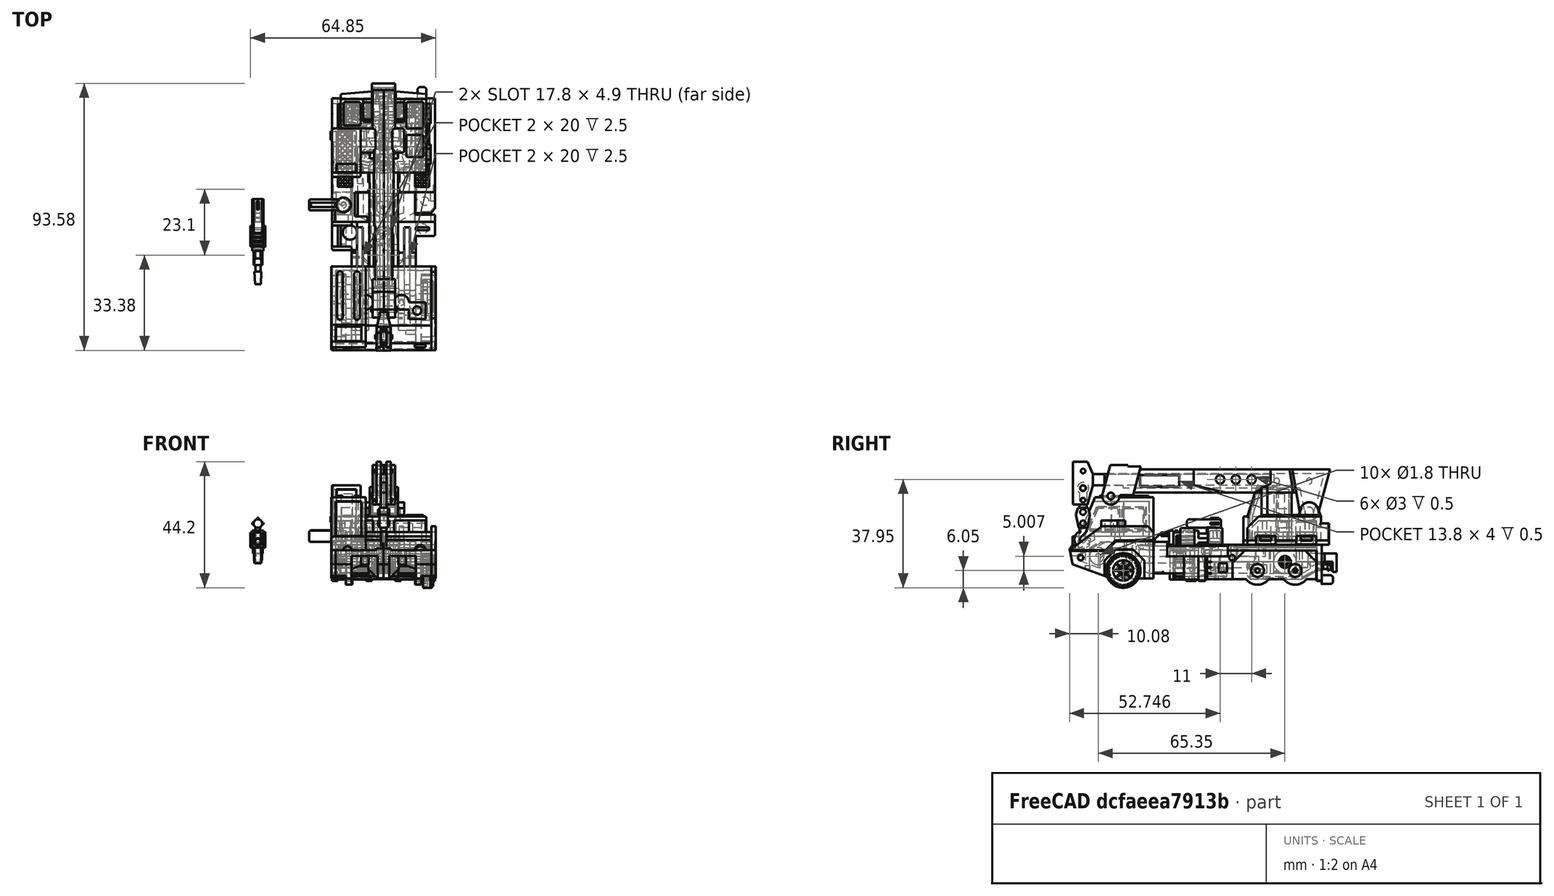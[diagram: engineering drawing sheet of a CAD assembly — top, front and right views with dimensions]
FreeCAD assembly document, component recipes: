
FREECAD ASSEMBLY — COMPONENT RECIPES ("Hook")

This assembly document has 27 components, labeled P0..P26 below (a component is one placed body or linked part). 27 of them carry a construction recipe — the FreeCAD feature program that regenerates the part from scratch, quoted from this document or its linked companion documents; the rest are supplied as boundary geometry only. No exploded tour is included for this assembly.
NOTE — this tour is split across 5 documents so each fits a 32k-token context. This is document 1: the component sections continue in the remaining 4 documents, each repeating the header above.
COMPONENT P0 — recipe-attached ("Rear_Torso", modeled in this document).
Construction recipe (the document's own serialized feature program — sketch geometry with constraints, then the solid features built on it; lengths are millimeters unless a unit is written):

FEATURE [Sketcher::SketchObject] Sketch
  ArcFitTolerance = 1e-06
  AttachmentSupport = -> [XY_Plane]
  FullyConstrained = true
  MakeInternals = false
  MapMode = 5
  sketch-geometry (4):
    g0: LineSegment StartX=0 StartY=0 StartZ=0 EndX=36 EndY=0 EndZ=0
    g1: LineSegment StartX=36 StartY=0 StartZ=0 EndX=36 EndY=43.2 EndZ=0
    g2: LineSegment StartX=36 StartY=43.2 StartZ=0 EndX=0 EndY=43.2 EndZ=0
    g3: LineSegment StartX=0 StartY=43.2 StartZ=0 EndX=0 EndY=0 EndZ=0
  constraints (11):
    c: Coincident(g0,g1)
    c: Coincident(g1,g2)
    c: Coincident(g2,g3)
    c: Coincident(g3,g0)
    c: Horizontal(g0)
    c: Horizontal(g2)
    c: Vertical(g1)
    c: Vertical(g3)
    c: Coincident(g0,g-1)
    c: DistanceY(g1,g1) = 43.2
    c: DistanceX(g2,g2) = 36
FEATURE [PartDesign::Pad] Pad
  Direction = (0,0,1)
  Length = 2
  Length2 = 10
  Profile = -> Sketch
  ReferenceAxis = -> Sketch [N_Axis]
  Refine = true
  Suppressed = false
  Type = 0
FEATURE [Sketcher::SketchObject] Sketch001
  ArcFitTolerance = 1e-06
  AttachmentSupport = -> [Pad]
  ExternalGeometry = -> [Pad]
  FullyConstrained = true
  MakeInternals = false
  MapMode = 5
  Placement = pos=(0,0,2) rot=(0,0,1;0rad)
  sketch-geometry (18):
    g0: LineSegment StartX=13.9 StartY=43.2 StartZ=0 EndX=13.9 EndY=41.4 EndZ=0
    g1: LineSegment StartX=13.9 StartY=41.4 StartZ=0 EndX=22.1 EndY=41.4 EndZ=0
    g2: LineSegment StartX=22.1 StartY=41.4 StartZ=0 EndX=22.1 EndY=43.2 EndZ=0
    g3: LineSegment StartX=22.1 StartY=43.2 StartZ=0 EndX=13.9 EndY=43.2 EndZ=0
    g4: LineSegment StartX=36 StartY=10.3 StartZ=0 EndX=23.6 EndY=10.3 EndZ=0
    g5: LineSegment StartX=23.6 StartY=10.3 StartZ=0 EndX=23.6 EndY=11.3 EndZ=0
    g6: ArcOfCircle CenterX=23.6 CenterY=12.55 CenterZ=0 NormalX=0 NormalY=0 NormalZ=1 AngleXU=0 Radius=1.25 StartAngle=1.5708 EndAngle=4.71239
    g7: LineSegment StartX=23.6 StartY=13.8 StartZ=0 EndX=23.6 EndY=18 EndZ=0
    g8: ArcOfCircle CenterX=18.1 CenterY=18 CenterZ=0 NormalX=0 NormalY=0 NormalZ=1 AngleXU=0 Radius=5.5 StartAngle=2e-16 EndAngle=3.14159
    g9: LineSegment StartX=12.6 StartY=18 StartZ=0 EndX=12.6 EndY=13.8 EndZ=0
    g10: ArcOfCircle CenterX=12.6 CenterY=12.55 CenterZ=0 NormalX=0 NormalY=0 NormalZ=1 AngleXU=0 Radius=1.25 StartAngle=4.71239 EndAngle=7.85398
    g11: LineSegment StartX=12.6 StartY=11.3 StartZ=0 EndX=12.6 EndY=10.3 EndZ=0
    g12: LineSegment StartX=12.6 StartY=10.3 StartZ=0 EndX=8 EndY=10.3 EndZ=0
    g13: LineSegment StartX=8 StartY=10.3 StartZ=0 EndX=8 EndY=1.8 EndZ=0
    g14: LineSegment StartX=8 StartY=1.8 StartZ=0 EndX=12.4 EndY=1.8 EndZ=0
    g15: LineSegment StartX=12.4 StartY=0 StartZ=0 EndX=36 EndY=0 EndZ=0
    g16: LineSegment StartX=36 StartY=0 StartZ=0 EndX=36 EndY=10.3 EndZ=0
    g17: LineSegment StartX=12.4 StartY=1.8 StartZ=0 EndX=12.4 EndY=0 EndZ=0
  constraints (58):
    c: Coincident(g0,g1)
    c: Coincident(g1,g2)
    c: Coincident(g2,g3)
    c: Coincident(g3,g0)
    c: Vertical(g0)
    c: Vertical(g2)
    c: Horizontal(g1)
    c: Horizontal(g3)
    c: PointOnObject(g0,g-3)
    c: DistanceX(g-3,g-3) = 36
    c: DistanceX(g-3,g0) = 13.9
    c: DistanceX(g2,g-3) = 13.9
    c: DistanceX(g0,g2) = 8.2
    c: DistanceY(g0,g0) = 1.8
    c: PointOnObject(g4,g-4)
    c: Horizontal(g4)
    c: DistanceY(g4,g-4) = 32.9
    c: DistanceX(g4,g4) = 12.4
    c: Coincident(g5,g4)
    c: Vertical(g5)
    c: Coincident(g6,g5)
    c: Coincident(g7,g6)
    c: Vertical(g7)
    c: Coincident(g8,g7)
    c: Coincident(g9,g8)
    c: Vertical(g9)
    c: Coincident(g10,g9)
    c: Coincident(g11,g10)
    c: Vertical(g11)
    c: Coincident(g12,g11)
    c: Horizontal(g12)
    c: Coincident(g13,g12)
    c: Vertical(g13)
    c: Coincident(g14,g13)
    c: Horizontal(g14)
    c: PointOnObject(g15,g-5)
    c: Coincident(g15,g-5)
    c: Coincident(g16,g15)
    c: Coincident(g16,g4)
    c: Diameter(g6) = 2.5
    c: Diameter(g10) = 2.5
    c: Diameter(g8) = 11
    c: DistanceX(g11,g4) = 11
    c: DistanceX(g6,g6) = 0
    c: DistanceX(g5,g6) = 0
    c: DistanceX(g10,g9) = 0
    c: DistanceX(g10,g10) = 0
    c: DistanceX(g-1,g13) = 8
    c: DistanceX(g13,g14) = 4.4
    c: Coincident(g17,g14)
    c: Coincident(g17,g15)
    c: Vertical(g17)
    c: DistanceY(g17,g17) = 1.8
    c: DistanceY(g15,g8) = 18
    c: DistanceY(g5,g5) = 1
    c: DistanceY(g11,g11) = 1
    c: DistanceY(g8,g7) = 0
    c: DistanceY(g12,g-6) = 32.9
FEATURE [PartDesign::Pocket] Pocket
  BaseFeature = -> Pad
  Direction = (0,0,-1)
  Length = 5
  Length2 = 5
  Profile = -> Sketch001
  ReferenceAxis = -> Sketch001 [N_Axis]
  Refine = true
  Suppressed = false
  Type = 0
FEATURE [Sketcher::SketchObject] Sketch002
  ArcFitTolerance = 1e-06
  AttachmentSupport = -> [Pocket]
  ExternalGeometry = -> [Pocket]
  FullyConstrained = true
  MakeInternals = false
  MapMode = 5
  Placement = pos=(0,0,2) rot=(0,0,1;0rad)
  sketch-geometry (8):
    g0: LineSegment StartX=2 StartY=41.2 StartZ=0 EndX=2 EndY=12.3 EndZ=0
    g1: LineSegment StartX=2 StartY=12.3 StartZ=0 EndX=7 EndY=12.3 EndZ=0
    g2: LineSegment StartX=7 StartY=12.3 StartZ=0 EndX=7 EndY=41.2 EndZ=0
    g3: LineSegment StartX=7 StartY=41.2 StartZ=0 EndX=2 EndY=41.2 EndZ=0
    g4: LineSegment StartX=29 StartY=41.2 StartZ=0 EndX=29 EndY=12.3 EndZ=0
    g5: LineSegment StartX=29 StartY=12.3 StartZ=0 EndX=34 EndY=12.3 EndZ=0
    g6: LineSegment StartX=34 StartY=12.3 StartZ=0 EndX=34 EndY=41.2 EndZ=0
    g7: LineSegment StartX=34 StartY=41.2 StartZ=0 EndX=29 EndY=41.2 EndZ=0
  constraints (25):
    c: Coincident(g0,g1)
    c: Coincident(g1,g2)
    c: Coincident(g2,g3)
    c: Coincident(g3,g0)
    c: Vertical(g0)
    c: Vertical(g2)
    c: Horizontal(g1)
    c: Horizontal(g3)
    c: Coincident(g4,g5)
    c: Coincident(g5,g6)
    c: Coincident(g6,g7)
    c: Coincident(g7,g4)
    c: Vertical(g4)
    c: Vertical(g6)
    c: Horizontal(g5)
    c: Horizontal(g7)
    c: DistanceX(g3,g3) = 5
    c: DistanceX(g7,g7) = 5
    c: DistanceX(g-6,g0) = 2
    c: DistanceX(g6,g-4) = 2
    c: DistanceY(g6,g-4) = 2
    c: DistanceY(g0,g-6) = 2
    c: DistanceY(g-3,g5) = 2
    c: DistanceY(g-7,g1) = 2
    c: DistanceY(g0,g0) = 28.9
FEATURE [PartDesign::Pocket] Pocket001
  BaseFeature = -> Pocket
  Direction = (0,0,-1)
  Length = 0.5
  Length2 = 5
  Profile = -> Sketch002
  ReferenceAxis = -> Sketch002 [N_Axis]
  Refine = true
  Suppressed = false
  Type = 0
FEATURE [Sketcher::SketchObject] Sketch003
  ArcFitTolerance = 1e-06
  AttachmentSupport = -> [Pocket001]
  ExternalGeometry = -> [Pocket001]
  FullyConstrained = true
  MakeInternals = false
  MapMode = 5
  Placement = pos=(0,0,1.5) rot=(0,0,1;0rad)
  sketch-geometry (36):
    g0: LineSegment StartX=30.625 StartY=41.2 StartZ=0 EndX=29.875 EndY=40.45 EndZ=0
    g1: LineSegment StartX=29.875 StartY=40.45 StartZ=0 EndX=30.625 EndY=39.7 EndZ=0
    g2: LineSegment StartX=30.625 StartY=39.7 StartZ=0 EndX=31.375 EndY=40.45 EndZ=0
    g3: LineSegment StartX=31.375 StartY=40.45 StartZ=0 EndX=30.625 EndY=41.2 EndZ=0
    g4: LineSegment [constr] StartX=29.875 StartY=40.45 StartZ=0 EndX=31.375 EndY=40.45 EndZ=0
    g5: LineSegment [constr] StartX=30.625 StartY=41.2 StartZ=0 EndX=30.625 EndY=39.7 EndZ=0
    g6: LineSegment StartX=31.625 StartY=40.45 StartZ=0 EndX=32.375 EndY=41.2 EndZ=0
    g7: LineSegment StartX=32.375 StartY=41.2 StartZ=0 EndX=33.125 EndY=40.45 EndZ=0
    g8: LineSegment StartX=33.125 StartY=40.45 StartZ=0 EndX=32.375 EndY=39.7 EndZ=0
    g9: LineSegment StartX=32.375 StartY=39.7 StartZ=0 EndX=31.625 EndY=40.45 EndZ=0
    g10: LineSegment [constr] StartX=32.375 StartY=41.2 StartZ=0 EndX=32.375 EndY=39.7 EndZ=0
    g11: LineSegment [constr] StartX=31.625 StartY=40.45 StartZ=0 EndX=33.125 EndY=40.45 EndZ=0
    g12: LineSegment StartX=29.625 StartY=40.45 StartZ=0 EndX=29 EndY=41.075 EndZ=0
    g13: LineSegment StartX=29 StartY=41.075 StartZ=0 EndX=29 EndY=39.825 EndZ=0
    g14: LineSegment StartX=29 StartY=39.825 StartZ=0 EndX=29.625 EndY=40.45 EndZ=0
    g15: LineSegment StartX=33.375 StartY=40.45 StartZ=0 EndX=34 EndY=41.075 EndZ=0
    g16: LineSegment StartX=34 StartY=41.075 StartZ=0 EndX=34 EndY=39.825 EndZ=0
    g17: LineSegment StartX=34 StartY=39.825 StartZ=0 EndX=33.375 EndY=40.45 EndZ=0
    g18: LineSegment StartX=3.625 StartY=41.2 StartZ=0 EndX=2.875 EndY=40.45 EndZ=0
    g19: LineSegment StartX=2.875 StartY=40.45 StartZ=0 EndX=3.625 EndY=39.7 EndZ=0
    g20: LineSegment StartX=3.625 StartY=39.7 StartZ=0 EndX=4.375 EndY=40.45 EndZ=0
    g21: LineSegment StartX=4.375 StartY=40.45 StartZ=0 EndX=3.625 EndY=41.2 EndZ=0
    g22: LineSegment [constr] StartX=2.875 StartY=40.45 StartZ=0 EndX=4.375 EndY=40.45 EndZ=0
    g23: LineSegment [constr] StartX=3.625 StartY=41.2 StartZ=0 EndX=3.625 EndY=39.7 EndZ=0
    g24: LineSegment StartX=4.625 StartY=40.45 StartZ=0 EndX=5.375 EndY=41.2 EndZ=0
    g25: LineSegment StartX=5.375 StartY=41.2 StartZ=0 EndX=6.125 EndY=40.45 EndZ=0
    g26: LineSegment StartX=6.125 StartY=40.45 StartZ=0 EndX=5.375 EndY=39.7 EndZ=0
    g27: LineSegment StartX=5.375 StartY=39.7 StartZ=0 EndX=4.625 EndY=40.45 EndZ=0
    g28: LineSegment [constr] StartX=5.375 StartY=41.2 StartZ=0 EndX=5.375 EndY=39.7 EndZ=0
    g29: LineSegment [constr] StartX=4.625 StartY=40.45 StartZ=0 EndX=6.125 EndY=40.45 EndZ=0
    g30: LineSegment StartX=2.625 StartY=40.45 StartZ=0 EndX=2 EndY=41.075 EndZ=0
    g31: LineSegment StartX=2 StartY=41.075 StartZ=0 EndX=2 EndY=39.825 EndZ=0
    g32: LineSegment StartX=2 StartY=39.825 StartZ=0 EndX=2.625 EndY=40.45 EndZ=0
    g33: LineSegment StartX=6.375 StartY=40.45 StartZ=0 EndX=7 EndY=41.075 EndZ=0
    g34: LineSegment StartX=7 StartY=41.075 StartZ=0 EndX=7 EndY=39.825 EndZ=0
    g35: LineSegment StartX=7 StartY=39.825 StartZ=0 EndX=6.375 EndY=40.45 EndZ=0
  constraints (101):
    c: DistanceX(g-3,g-3) = 5
    c: Coincident(g2,g1)
    c: Coincident(g3,g2)
    c: Coincident(g3,g0)
    c: Coincident(g4,g0)
    c: Coincident(g4,g2)
    c: Coincident(g5,g0)
    c: Coincident(g5,g1)
    c: Horizontal(g4)
    c: Vertical(g5)
    c: DistanceX(g4,g4) = 1.5
    c: Angle(g3,g2) = 1.5708
    c: Angle(g0,g3) = 1.5708
    c: Angle(g2,g1) = 1.5708
    c: Coincident(g1,g0)
    c: Coincident(g7,g6)
    c: Coincident(g8,g7)
    c: Coincident(g9,g8)
    c: Coincident(g9,g6)
    c: Coincident(g10,g6)
    c: Coincident(g10,g8)
    c: Coincident(g11,g6)
    c: Coincident(g11,g7)
    c: Horizontal(g11)
    c: Vertical(g10)
    c: DistanceX(g11,g11) = 1.5
    c: Angle(g7,g8) = 1.5708
    c: Angle(g6,g7) = 1.5708
    c: Angle(g8,g9) = 1.5708
    c: DistanceX(g2,g6) = 0.25
    c: DistanceY(g2,g6) = 0
    c: Coincident(g13,g12)
    c: Vertical(g13)
    c: Coincident(g14,g13)
    c: Coincident(g14,g12)
    c: DistanceX(g12,g0) = 0.25
    c: DistanceY(g12,g0) = 0
    c: Angle(g12,g14) = 1.5708
    c: Coincident(g16,g15)
    c: Vertical(g16)
    c: Coincident(g17,g16)
    c: Coincident(g17,g15)
    c: DistanceX(g7,g15) = 0.25
    c: DistanceY(g15,g7) = 0
    c: Angle(g17,g15) = 1.5708
    c: Angle(g13,g12) = 0.785398
    c: Angle(g15,g16) = 0.785398
    c: DistanceX(g15,g15) = 0.625
    c: DistanceX(g12,g12) = 0.625
    c: Coincident(g20,g19)
    c: Coincident(g21,g20)
    c: Coincident(g21,g18)
    c: Coincident(g22,g18)
    c: Coincident(g22,g20)
    c: Coincident(g23,g18)
    c: Coincident(g23,g19)
    c: Horizontal(g22)
    c: Vertical(g23)
    c: DistanceX(g22,g22) = 1.5
    c: Angle(g21,g20) = 1.5708
    c: Angle(g18,g21) = 1.5708
    c: Angle(g20,g19) = 1.5708
    c: Coincident(g19,g18)
    c: Coincident(g25,g24)
    c: Coincident(g26,g25)
    c: Coincident(g27,g26)
    c: Coincident(g27,g24)
    c: Coincident(g28,g24)
    c: Coincident(g28,g26)
    c: Coincident(g29,g24)
    c: Coincident(g29,g25)
    c: Horizontal(g29)
    c: Vertical(g28)
    c: DistanceX(g29,g29) = 1.5
    c: Angle(g25,g26) = 1.5708
    c: Angle(g24,g25) = 1.5708
    c: Angle(g26,g27) = 1.5708
    c: DistanceX(g20,g24) = 0.25
    c: DistanceY(g20,g24) = 0
    c: Coincident(g31,g30)
    c: Vertical(g31)
    c: Coincident(g32,g31)
    c: Coincident(g32,g30)
    c: DistanceX(g30,g18) = 0.25
    c: DistanceY(g30,g18) = 0
    c: Angle(g30,g32) = 1.5708
    c: Coincident(g34,g33)
    c: Vertical(g34)
    c: Coincident(g35,g34)
    c: Coincident(g35,g33)
    c: DistanceX(g25,g33) = 0.25
    c: DistanceY(g33,g25) = 0
    c: Angle(g35,g33) = 1.5708
    c: Angle(g31,g30) = 0.785398
    c: Angle(g33,g34) = 0.785398
    c: DistanceX(g33,g33) = 0.625
    c: DistanceX(g30,g30) = 0.625
    c: PointOnObject(g0,g-5)
    c: PointOnObject(g12,g-6)
    c: PointOnObject(g18,g-3)
    c: PointOnObject(g30,g-4)
FEATURE [PartDesign::Pocket] Pocket002
  BaseFeature = -> Pocket001
  Direction = (0,0,-1)
  Length = 0.5
  Length2 = 5
  Profile = -> Sketch003
  ReferenceAxis = -> Sketch003 [N_Axis]
  Refine = true
  Suppressed = false
  Type = 0
FEATURE [PartDesign::LinearPattern] LinearPattern
  BaseFeature = -> Pocket002
  Direction = -> Sketch003 [V_Axis]
  Length = 27.398
  Mode = 1
  Occurrences = 15
  Offset = 1.957
  Originals = -> [Pocket002]
  Refine = true
  Reversed = true
  Suppressed = false
  TransformMode = 0
FEATURE [Sketcher::SketchObject] Sketch004
  ArcFitTolerance = 1e-06
  AttachmentSupport = -> [LinearPattern]
  ExternalGeometry = -> [LinearPattern]
  FullyConstrained = true
  MakeInternals = false
  MapMode = 5
  Placement = pos=(0,0,1.5) rot=(0,0,1;0rad)
  sketch-geometry (36):
    g0: LineSegment StartX=2.125 StartY=41.2 StartZ=0 EndX=3.375 EndY=41.2 EndZ=0
    g1: LineSegment StartX=3.375 StartY=41.2 StartZ=0 EndX=2.75 EndY=40.575 EndZ=0
    g2: LineSegment StartX=2.75 StartY=40.575 StartZ=0 EndX=2.125 EndY=41.2 EndZ=0
    g3: LineSegment StartX=3.875 StartY=41.2 StartZ=0 EndX=5.125 EndY=41.2 EndZ=0
    g4: LineSegment StartX=5.125 StartY=41.2 StartZ=0 EndX=4.5 EndY=40.575 EndZ=0
    g5: LineSegment StartX=4.5 StartY=40.575 StartZ=0 EndX=3.875 EndY=41.2 EndZ=0
    g6: LineSegment StartX=5.625 StartY=41.2 StartZ=0 EndX=6.875 EndY=41.2 EndZ=0
    g7: LineSegment StartX=6.875 StartY=41.2 StartZ=0 EndX=6.25 EndY=40.575 EndZ=0
    g8: LineSegment StartX=6.25 StartY=40.575 StartZ=0 EndX=5.625 EndY=41.2 EndZ=0
    g9: LineSegment StartX=6.877 StartY=12.3 StartZ=0 EndX=5.623 EndY=12.3 EndZ=0
    g10: LineSegment StartX=5.623 StartY=12.3 StartZ=0 EndX=6.25 EndY=12.927 EndZ=0
    g11: LineSegment StartX=6.25 StartY=12.927 StartZ=0 EndX=6.877 EndY=12.3 EndZ=0
    g12: LineSegment StartX=3.873 StartY=12.3 StartZ=0 EndX=5.127 EndY=12.3 EndZ=0
    g13: LineSegment StartX=5.127 StartY=12.3 StartZ=0 EndX=4.5 EndY=12.927 EndZ=0
    g14: LineSegment StartX=4.5 StartY=12.927 StartZ=0 EndX=3.873 EndY=12.3 EndZ=0
    g15: LineSegment StartX=3.377 StartY=12.3 StartZ=0 EndX=2.123 EndY=12.3 EndZ=0
    g16: LineSegment StartX=2.123 StartY=12.3 StartZ=0 EndX=2.75 EndY=12.927 EndZ=0
    g17: LineSegment StartX=2.75 StartY=12.927 StartZ=0 EndX=3.377 EndY=12.3 EndZ=0
    g18: LineSegment StartX=29.125 StartY=41.2 StartZ=0 EndX=30.375 EndY=41.2 EndZ=0
    g19: LineSegment StartX=30.375 StartY=41.2 StartZ=0 EndX=29.75 EndY=40.575 EndZ=0
    g20: LineSegment StartX=29.75 StartY=40.575 StartZ=0 EndX=29.125 EndY=41.2 EndZ=0
    g21: LineSegment StartX=30.875 StartY=41.2 StartZ=0 EndX=32.125 EndY=41.2 EndZ=0
    g22: LineSegment StartX=32.125 StartY=41.2 StartZ=0 EndX=31.5 EndY=40.575 EndZ=0
    g23: LineSegment StartX=31.5 StartY=40.575 StartZ=0 EndX=30.875 EndY=41.2 EndZ=0
    g24: LineSegment StartX=32.625 StartY=41.2 StartZ=0 EndX=33.875 EndY=41.2 EndZ=0
    g25: LineSegment StartX=33.875 StartY=41.2 StartZ=0 EndX=33.25 EndY=40.575 EndZ=0
    g26: LineSegment StartX=33.25 StartY=40.575 StartZ=0 EndX=32.625 EndY=41.2 EndZ=0
    g27: LineSegment StartX=29.123 StartY=12.3 StartZ=0 EndX=30.377 EndY=12.3 EndZ=0
    g28: LineSegment StartX=30.377 StartY=12.3 StartZ=0 EndX=29.75 EndY=12.927 EndZ=0
    g29: LineSegment StartX=29.75 StartY=12.927 StartZ=0 EndX=29.123 EndY=12.3 EndZ=0
    g30: LineSegment StartX=30.873 StartY=12.3 StartZ=0 EndX=32.127 EndY=12.3 EndZ=0
    g31: LineSegment StartX=32.127 StartY=12.3 StartZ=0 EndX=31.5 EndY=12.927 EndZ=0
    g32: LineSegment StartX=31.5 StartY=12.927 StartZ=0 EndX=30.873 EndY=12.3 EndZ=0
    g33: LineSegment StartX=32.623 StartY=12.3 StartZ=0 EndX=33.877 EndY=12.3 EndZ=0
    g34: LineSegment StartX=33.877 StartY=12.3 StartZ=0 EndX=33.25 EndY=12.927 EndZ=0
    g35: LineSegment StartX=33.25 StartY=12.927 StartZ=0 EndX=32.623 EndY=12.3 EndZ=0
  constraints (109):
    c: PointOnObject(g0,g-5)
    c: PointOnObject(g0,g-5)
    c: Coincident(g1,g0)
    c: Coincident(g2,g1)
    c: Coincident(g2,g0)
    c: DistanceX(g-4,g-3) = 0.25
    c: DistanceX(g-4,g1) = 0.125
    c: DistanceY(g-4,g1) = 0.125
    c: Parallel(g1,g-3)
    c: Parallel(g2,g-4)
    c: PointOnObject(g3,g-6)
    c: PointOnObject(g3,g-6)
    c: Coincident(g4,g3)
    c: Coincident(g5,g4)
    c: Coincident(g5,g3)
    c: PointOnObject(g6,g-9)
    c: PointOnObject(g6,g-9)
    c: Coincident(g7,g6)
    c: Coincident(g8,g7)
    c: Coincident(g8,g6)
    c: DistanceX(g-7,g4) = 0.125
    c: DistanceX(g-10,g7) = 0.125
    c: Parallel(g-7,g5)
    c: Parallel(g4,g-8)
    c: Parallel(g-10,g8)
    c: Parallel(g7,g-11)
    c: DistanceY(g-7,g4) = 0.125
    c: DistanceY(g-10,g7) = 0.125
    c: PointOnObject(g9,g-14)
    c: PointOnObject(g9,g-14)
    c: Coincident(g10,g9)
    c: Coincident(g11,g10)
    c: Coincident(g11,g9)
    c: PointOnObject(g12,g-14)
    c: PointOnObject(g12,g-14)
    c: Coincident(g13,g12)
    c: Coincident(g14,g13)
    c: Coincident(g14,g12)
    c: PointOnObject(g15,g-14)
    c: PointOnObject(g15,g-14)
    c: Coincident(g16,g15)
    c: Coincident(g17,g16)
    c: Coincident(g17,g15)
    c: Parallel(g-13,g16)
    c: Parallel(g17,g-12)
    c: Parallel(g-16,g14)
    c: Parallel(g13,g-15)
    c: Parallel(g-17,g10)
    c: Parallel(g11,g-18)
    c: DistanceX(g-17,g10) = 0.125
    c: DistanceX(g-16,g13) = 0.125
    c: DistanceX(g16,g-12) = 0.125
    c: DistanceY(g16,g-13) = 0.125
    c: DistanceY(g13,g-16) = 0.125
    c: DistanceY(g10,g-17) = 0.125
    c: PointOnObject(g18,g-19)
    c: PointOnObject(g18,g-19)
    c: Coincident(g19,g18)
    c: Coincident(g20,g19)
    c: Coincident(g20,g18)
    c: PointOnObject(g21,g-22)
    c: PointOnObject(g21,g-22)
    c: Coincident(g22,g21)
    c: Coincident(g23,g22)
    c: Coincident(g23,g21)
    c: PointOnObject(g24,g-25)
    c: PointOnObject(g24,g-25)
    c: Coincident(g25,g24)
    c: Coincident(g26,g25)
    c: Coincident(g26,g24)
    c: Parallel(g-26,g26)
    c: Parallel(g25,g-27)
    c: Parallel(g22,g-24)
    c: Parallel(g23,g-23)
    c: Parallel(g-21,g19)
    c: Parallel(g20,g-20)
    c: DistanceX(g-20,g19) = 0.125
    c: DistanceX(g-23,g22) = 0.125
    c: DistanceX(g-26,g25) = 0.125
    c: DistanceY(g-26,g25) = 0.125
    c: DistanceY(g-23,g22) = 0.125
    c: DistanceY(g-20,g19) = 0.125
    c: PointOnObject(g27,g-30)
    c: PointOnObject(g27,g-30)
    c: Coincident(g28,g27)
    c: Coincident(g29,g28)
    c: Coincident(g29,g27)
    c: PointOnObject(g30,g-30)
    c: PointOnObject(g30,g-30)
    c: Coincident(g31,g30)
    c: Coincident(g32,g31)
    c: Coincident(g32,g30)
    c: PointOnObject(g33,g-30)
    c: PointOnObject(g33,g-30)
    c: Coincident(g34,g33)
    c: Coincident(g35,g34)
    c: Coincident(g35,g33)
    c: Parallel(g29,g-28)
    c: Parallel(g28,g-29)
    c: Parallel(g32,g-31)
    c: Parallel(g31,g-32)
    c: Parallel(g35,g-33)
    c: Parallel(g34,g-34)
    c: DistanceX(g-28,g28) = 0.125
    c: DistanceX(g-31,g31) = 0.125
    c: DistanceX(g-33,g34) = 0.125
    c: DistanceY(g28,g-28) = 0.125
    c: DistanceY(g31,g-31) = 0.125
    c: DistanceY(g34,g-33) = 0.125
FEATURE [PartDesign::Pocket] Pocket003
  BaseFeature = -> LinearPattern
  Direction = (0,0,-1)
  Length = 0.5
  Length2 = 5
  Profile = -> Sketch004
  ReferenceAxis = -> Sketch004 [N_Axis]
  Refine = true
  Suppressed = false
  Type = 0
FEATURE [Sketcher::SketchObject] Sketch005
  ArcFitTolerance = 1e-06
  AttachmentSupport = -> [Pocket003]
  ExternalGeometry = -> [Pocket003]
  FullyConstrained = true
  MakeInternals = false
  MapMode = 5
  Placement = pos=(0,0,1.5) rot=(0,0,1;0rad)
  sketch-geometry (36):
    g0: LineSegment StartX=2.75 StartY=40.22 StartZ=0 EndX=2 EndY=39.47 EndZ=0
    g1: LineSegment StartX=2 StartY=39.47 StartZ=0 EndX=2.75 EndY=38.72 EndZ=0
    g2: LineSegment StartX=2.75 StartY=38.72 StartZ=0 EndX=3.5 EndY=39.47 EndZ=0
    g3: LineSegment StartX=3.5 StartY=39.47 StartZ=0 EndX=2.75 EndY=40.22 EndZ=0
    g4: LineSegment StartX=4.5 StartY=40.22 StartZ=0 EndX=3.75 EndY=39.47 EndZ=0
    g5: LineSegment StartX=3.75 StartY=39.47 StartZ=0 EndX=4.5 EndY=38.72 EndZ=0
    g6: LineSegment StartX=4.5 StartY=38.72 StartZ=0 EndX=5.25 EndY=39.47 EndZ=0
    g7: LineSegment StartX=5.25 StartY=39.47 StartZ=0 EndX=4.5 EndY=40.22 EndZ=0
    g8: LineSegment StartX=6.25 StartY=40.22 StartZ=0 EndX=5.5 EndY=39.47 EndZ=0
    g9: LineSegment StartX=5.5 StartY=39.47 StartZ=0 EndX=6.25 EndY=38.72 EndZ=0
    g10: LineSegment StartX=6.25 StartY=38.72 StartZ=0 EndX=7 EndY=39.47 EndZ=0
    g11: LineSegment StartX=7 StartY=39.47 StartZ=0 EndX=6.25 EndY=40.22 EndZ=0
    g12: LineSegment [constr] StartX=6.25 StartY=40.22 StartZ=0 EndX=6.25 EndY=38.72 EndZ=0
    g13: LineSegment [constr] StartX=4.5 StartY=40.22 StartZ=0 EndX=4.5 EndY=38.72 EndZ=0
    g14: LineSegment [constr] StartX=2.75 StartY=40.22 StartZ=0 EndX=2.75 EndY=38.72 EndZ=0
    g15: LineSegment [constr] StartX=3.5 StartY=39.47 StartZ=0 EndX=2 EndY=39.47 EndZ=0
    g16: LineSegment [constr] StartX=5.25 StartY=39.47 StartZ=0 EndX=3.75 EndY=39.47 EndZ=0
    g17: LineSegment [constr] StartX=7 StartY=39.47 StartZ=0 EndX=5.5 EndY=39.47 EndZ=0
    g18: LineSegment StartX=29.75 StartY=40.22 StartZ=0 EndX=29 EndY=39.47 EndZ=0
    g19: LineSegment StartX=29 StartY=39.47 StartZ=0 EndX=29.75 EndY=38.72 EndZ=0
    g20: LineSegment StartX=29.75 StartY=38.72 StartZ=0 EndX=30.5 EndY=39.47 EndZ=0
    g21: LineSegment StartX=30.5 StartY=39.47 StartZ=0 EndX=29.75 EndY=40.22 EndZ=0
    g22: LineSegment StartX=31.5 StartY=40.22 StartZ=0 EndX=30.75 EndY=39.47 EndZ=0
    g23: LineSegment StartX=30.75 StartY=39.47 StartZ=0 EndX=31.5 EndY=38.72 EndZ=0
    g24: LineSegment StartX=31.5 StartY=38.72 StartZ=0 EndX=32.25 EndY=39.47 EndZ=0
    g25: LineSegment StartX=32.25 StartY=39.47 StartZ=0 EndX=31.5 EndY=40.22 EndZ=0
    g26: LineSegment StartX=33.25 StartY=40.22 StartZ=0 EndX=32.5 EndY=39.47 EndZ=0
    g27: LineSegment StartX=32.5 StartY=39.47 StartZ=0 EndX=33.25 EndY=38.72 EndZ=0
    g28: LineSegment StartX=33.25 StartY=38.72 StartZ=0 EndX=34 EndY=39.47 EndZ=0
    g29: LineSegment StartX=34 StartY=39.47 StartZ=0 EndX=33.25 EndY=40.22 EndZ=0
    g30: LineSegment [constr] StartX=30.5 StartY=39.47 StartZ=0 EndX=29 EndY=39.47 EndZ=0
    g31: LineSegment [constr] StartX=29.75 StartY=40.22 StartZ=0 EndX=29.75 EndY=38.72 EndZ=0
    g32: LineSegment [constr] StartX=31.5 StartY=40.22 StartZ=0 EndX=31.5 EndY=38.72 EndZ=0
    g33: LineSegment [constr] StartX=32.25 StartY=39.47 StartZ=0 EndX=30.75 EndY=39.47 EndZ=0
    g34: LineSegment [constr] StartX=33.25 StartY=40.22 StartZ=0 EndX=33.25 EndY=38.72 EndZ=0
    g35: LineSegment [constr] StartX=34 StartY=39.47 StartZ=0 EndX=32.5 EndY=39.47 EndZ=0
  constraints (97):
    c: Coincident(g1,g0)
    c: Coincident(g2,g1)
    c: Coincident(g3,g2)
    c: Coincident(g3,g0)
    c: Coincident(g5,g4)
    c: Coincident(g6,g5)
    c: Coincident(g7,g6)
    c: Coincident(g7,g4)
    c: Coincident(g9,g8)
    c: Coincident(g10,g9)
    c: Coincident(g11,g10)
    c: Coincident(g11,g8)
    c: Coincident(g12,g8)
    c: Coincident(g12,g9)
    c: Vertical(g12)
    c: Coincident(g13,g4)
    c: Coincident(g13,g5)
    c: Vertical(g13)
    c: Coincident(g14,g0)
    c: Coincident(g14,g1)
    c: Coincident(g15,g2)
    c: Coincident(g15,g0)
    c: Horizontal(g15)
    c: Coincident(g16,g6)
    c: Coincident(g16,g4)
    c: Horizontal(g16)
    c: Coincident(g17,g10)
    c: Coincident(g17,g8)
    c: Horizontal(g17)
    c: Vertical(g14)
    c: DistanceX(g15,g15) = 1.5
    c: DistanceX(g16,g16) = 1.5
    c: DistanceX(g17,g17) = 1.5
    c: Angle(g3,g2) = 1.5708
    c: Angle(g0,g3) = 1.5708
    c: Angle(g2,g1) = 1.5708
    c: Angle(g7,g6) = 1.5708
    c: Angle(g4,g7) = 1.5708
    c: Angle(g6,g5) = 1.5708
    c: Angle(g11,g10) = 1.5708
    c: Angle(g8,g11) = 1.5708
    c: Angle(g10,g9) = 1.5708
    c: PointOnObject(g10,g-15)
    c: PointOnObject(g0,g-16)
    c: DistanceY(g0,g-3) = 0.23
    c: DistanceY(g4,g-8) = 0.23
    c: DistanceY(g8,g-12) = 0.23
    c: DistanceX(g4,g-18) = 0
    c: DistanceY(g-6,g1) = 0.227
    c: Coincident(g19,g18)
    c: Coincident(g20,g19)
    c: Coincident(g21,g20)
    c: Coincident(g21,g18)
    c: Coincident(g23,g22)
    c: Coincident(g24,g23)
    c: Coincident(g25,g24)
    c: Coincident(g25,g22)
    c: Coincident(g27,g26)
    c: Coincident(g28,g27)
    c: Coincident(g29,g28)
    c: Coincident(g29,g26)
    c: Coincident(g30,g20)
    c: Coincident(g30,g18)
    c: Horizontal(g30)
    c: Coincident(g31,g18)
    c: Coincident(g31,g19)
    c: Coincident(g32,g22)
    c: Coincident(g32,g23)
    c: Vertical(g32)
    c: Coincident(g33,g24)
    c: Coincident(g33,g22)
    c: Horizontal(g33)
    c: Coincident(g34,g26)
    c: Coincident(g34,g27)
    c: Vertical(g34)
    c: Coincident(g35,g28)
    c: Coincident(g35,g26)
    c: Horizontal(g35)
    c: Vertical(g31)
    c: DistanceX(g30,g30) = 1.5
    c: DistanceX(g33,g33) = 1.5
    c: DistanceX(g35,g35) = 1.5
    c: Angle(g29,g28) = 1.5708
    c: Angle(g25,g24) = 1.5708
    c: Angle(g21,g20) = 1.5708
    c: Angle(g18,g21) = 1.5708
    c: Angle(g20,g19) = 1.5708
    c: Angle(g22,g25) = 1.5708
    c: Angle(g24,g23) = 1.5708
    c: Angle(g26,g29) = 1.5708
    c: Angle(g28,g27) = 1.5708
    c: PointOnObject(g18,g-32)
    c: PointOnObject(g28,g-33)
    c: DistanceX(g22,g-35) = 0
    c: DistanceY(g18,g-20) = 0.23
    c: DistanceY(g22,g-25) = 0.23
    c: DistanceY(g26,g-29) = 0.23
FEATURE [PartDesign::Pocket] Pocket004
  BaseFeature = -> Pocket003
  Direction = (0,0,-1)
  Length = 0.5
  Length2 = 5
  Profile = -> Sketch005
  ReferenceAxis = -> Sketch005 [N_Axis]
  Refine = true
  Suppressed = false
  Type = 0
FEATURE [PartDesign::LinearPattern] LinearPattern001
  BaseFeature = -> Pocket004
  Direction = -> Sketch005 [V_Axis]
  Length = 25.441
  Mode = 1
  Occurrences = 14
  Offset = 1.957
  Originals = -> [Pocket004]
  Refine = true
  Reversed = true
  Suppressed = false
  TransformMode = 0
FEATURE [Sketcher::SketchObject] Sketch006
  ArcFitTolerance = 1e-06
  AttachmentSupport = -> [LinearPattern001]
  ExternalGeometry = -> [LinearPattern001]
  FullyConstrained = true
  MakeInternals = false
  MapMode = 5
  Placement = pos=(0,0,2) rot=(0,0,1;0rad)
  sketch-geometry (1):
    g0: Circle CenterX=18.1 CenterY=30.5 CenterZ=0 NormalX=0 NormalY=0 NormalZ=1 AngleXU=0 Radius=5.5
  constraints (3):
    c: DistanceX(g0,g-3) = 0
    c: Diameter(g0) = 11
    c: DistanceY(g0,g-4) = 12.7
FEATURE [PartDesign::Pad] Pad001
  BaseFeature = -> LinearPattern001
  Direction = (0,0,1)
  Length = 3
  Length2 = 10
  Profile = -> Sketch006
  ReferenceAxis = -> Sketch006 [N_Axis]
  Refine = true
  Suppressed = false
  Type = 0
FEATURE [Sketcher::SketchObject] Sketch007
  ArcFitTolerance = 1e-06
  AttachmentSupport = -> [Pad001]
  ExternalGeometry = -> [Pad001]
  FullyConstrained = true
  MakeInternals = false
  MapMode = 5
  Placement = pos=(0,0,5) rot=(0,0,1;0rad)
  sketch-geometry (1):
    g0: Circle CenterX=18.1 CenterY=30.5 CenterZ=0 NormalX=0 NormalY=0 NormalZ=1 AngleXU=0 Radius=2.5
  constraints (2):
    c: Coincident(g0,g-3)
    c: Diameter(g0) = 5
FEATURE [PartDesign::Pocket] Pocket005
  BaseFeature = -> Pad001
  Direction = (0,0,-1)
  Length = 5
  Length2 = 5
  Profile = -> Sketch007
  ReferenceAxis = -> Sketch007 [N_Axis]
  Refine = true
  Suppressed = false
  Type = 0
FEATURE [Sketcher::SketchObject] Sketch008
  ArcFitTolerance = 1e-06
  AttachmentSupport = -> [Pocket005]
  ExternalGeometry = -> [Pocket005]
  FullyConstrained = true
  MakeInternals = false
  MapMode = 5
  Placement = pos=(0,0,0) rot=(1,0,0;3.14159rad)
  sketch-geometry (1):
    g0: Circle CenterX=18.1 CenterY=-30.5 CenterZ=0 NormalX=0 NormalY=0 NormalZ=1 AngleXU=0 Radius=3.45
  constraints (2):
    c: Coincident(g0,g-3)
    c: Diameter(g0) = 6.9
FEATURE [PartDesign::Pocket] Pocket006
  BaseFeature = -> Pocket005
  Direction = (0,0,1)
  Length = 3.1
  Length2 = 5
  Profile = -> Sketch008
  ReferenceAxis = -> Sketch008 [N_Axis]
  Refine = true
  Suppressed = false
  Type = 0
FEATURE [Sketcher::SketchObject] Sketch009
  ArcFitTolerance = 1e-06
  AttachmentSupport = -> [Pocket006]
  ExternalGeometry = -> [Pocket006]
  FullyConstrained = true
  MakeInternals = false
  MapMode = 5
  Placement = pos=(0,0,0) rot=(1,0,0;3.14159rad)
  sketch-geometry (8):
    g0: LineSegment StartX=0 StartY=-43.2 StartZ=0 EndX=13.9 EndY=-43.2 EndZ=0
    g1: LineSegment StartX=13.9 StartY=-43.2 StartZ=0 EndX=13.9 EndY=-41.4 EndZ=0
    g2: LineSegment StartX=13.9 StartY=-41.4 StartZ=0 EndX=0 EndY=-41.4 EndZ=0
    g3: LineSegment StartX=0 StartY=-41.4 StartZ=0 EndX=0 EndY=-43.2 EndZ=0
    g4: LineSegment StartX=36 StartY=-43.2 StartZ=0 EndX=36 EndY=-41.4 EndZ=0
    g5: LineSegment StartX=36 StartY=-41.4 StartZ=0 EndX=22.1 EndY=-41.4 EndZ=0
    g6: LineSegment StartX=22.1 StartY=-41.4 StartZ=0 EndX=22.1 EndY=-43.2 EndZ=0
    g7: LineSegment StartX=22.1 StartY=-43.2 StartZ=0 EndX=36 EndY=-43.2 EndZ=0
  constraints (20):
    c: Coincident(g0,g1)
    c: Coincident(g1,g2)
    c: Coincident(g2,g3)
    c: Coincident(g3,g0)
    c: Horizontal(g0)
    c: Horizontal(g2)
    c: Vertical(g1)
    c: Vertical(g3)
    c: Coincident(g0,g-8)
    c: Coincident(g1,g-6)
    c: Coincident(g4,g5)
    c: Coincident(g5,g6)
    c: Coincident(g6,g7)
    c: Coincident(g7,g4)
    c: Vertical(g4)
    c: Vertical(g6)
    c: Horizontal(g5)
    c: Horizontal(g7)
    c: Coincident(g4,g-4)
    c: Coincident(g5,g-5)
FEATURE [PartDesign::Pad] Pad002
  BaseFeature = -> Pocket006
  Direction = (0,0,-1)
  Length = 10.7
  Length2 = 10
  Profile = -> Sketch009
  ReferenceAxis = -> Sketch009 [N_Axis]
  Refine = true
  Suppressed = false
  Type = 0
FEATURE [Sketcher::SketchObject] Sketch010
  ArcFitTolerance = 1e-06
  AttachmentSupport = -> [Pad002]
  ExternalGeometry = -> [Pad002]
  FullyConstrained = true
  MakeInternals = false
  MapMode = 5
  Placement = pos=(0,0,-10.7) rot=(1,0,0;3.14159rad)
  sketch-geometry (8):
    g0: LineSegment StartX=2 StartY=-41.4 StartZ=0 EndX=2 EndY=-43.2 EndZ=0
    g1: LineSegment StartX=2 StartY=-43.2 StartZ=0 EndX=11.9 EndY=-43.2 EndZ=0
    g2: LineSegment StartX=11.9 StartY=-43.2 StartZ=0 EndX=11.9 EndY=-41.4 EndZ=0
    g3: LineSegment StartX=11.9 StartY=-41.4 StartZ=0 EndX=2 EndY=-41.4 EndZ=0
    g4: LineSegment StartX=24.1 StartY=-41.4 StartZ=0 EndX=24.1 EndY=-43.2 EndZ=0
    g5: LineSegment StartX=24.1 StartY=-43.2 StartZ=0 EndX=34 EndY=-43.2 EndZ=0
    g6: LineSegment StartX=34 StartY=-43.2 StartZ=0 EndX=34 EndY=-41.4 EndZ=0
    g7: LineSegment StartX=34 StartY=-41.4 StartZ=0 EndX=24.1 EndY=-41.4 EndZ=0
  constraints (24):
    c: Coincident(g0,g1)
    c: Coincident(g1,g2)
    c: Coincident(g2,g3)
    c: Coincident(g3,g0)
    c: Vertical(g0)
    c: Vertical(g2)
    c: Horizontal(g1)
    c: Horizontal(g3)
    c: PointOnObject(g0,g-8)
    c: PointOnObject(g1,g-9)
    c: Coincident(g4,g5)
    c: Coincident(g5,g6)
    c: Coincident(g6,g7)
    c: Coincident(g7,g4)
    c: Vertical(g4)
    c: Vertical(g6)
    c: Horizontal(g5)
    c: Horizontal(g7)
    c: PointOnObject(g4,g-3)
    c: PointOnObject(g5,g-5)
    c: DistanceX(g-6,g4) = 2
    c: DistanceX(g6,g-4) = 2
    c: DistanceX(g2,g-8) = 2
    c: DistanceX(g-10,g0) = 2
FEATURE [PartDesign::Pocket] Pocket007
  BaseFeature = -> Pad002
  Direction = (0,0,1)
  Length = 0.5
  Length2 = 5
  Profile = -> Sketch010
  ReferenceAxis = -> Sketch010 [N_Axis]
  Refine = true
  Suppressed = false
  Type = 0
FEATURE [Sketcher::SketchObject] Sketch011
  ArcFitTolerance = 1e-06
  AttachmentSupport = -> [Pocket007]
  ExternalGeometry = -> [Pocket007]
  FullyConstrained = true
  MakeInternals = false
  MapMode = 5
  Placement = pos=(0,43.2,0) rot=(0,0.707107,0.707107;3.14159rad)
  sketch-geometry (1):
    g0: Circle CenterX=-31.45 CenterY=-10.2 CenterZ=0 NormalX=0 NormalY=0 NormalZ=1 AngleXU=0 Radius=1.55
  constraints (3):
    c: PointOnObject(g0,g-3)
    c: Diameter(g0) = 3.1
    c: DistanceX(g-4,g0) = 4.55
FEATURE [PartDesign::Pad] Pad003
  BaseFeature = -> Pocket007
  Direction = (0,1,-2e-16)
  Length = 4
  Length2 = 10
  Profile = -> Sketch011
  ReferenceAxis = -> Sketch011 [N_Axis]
  Refine = true
  Suppressed = false
  Type = 0
FEATURE [PartDesign::Fillet] Fillet
  Base = -> Pad003 [Edge479]
  BaseFeature = -> Pad003
  Radius = 1
  Refine = true
  SupportTransform = false
  Suppressed = false
  UseAllEdges = false
FEATURE [Sketcher::SketchObject] Sketch012
  ArcFitTolerance = 1e-06
  AttachmentSupport = -> [Fillet]
  ExternalGeometry = -> [Fillet]
  FullyConstrained = true
  MakeInternals = false
  MapMode = 5
  Placement = pos=(0,0,0) rot=(1,0,0;3.14159rad)
  sketch-geometry (4):
    g0: LineSegment StartX=11.9 StartY=-41.4 StartZ=0 EndX=24.1 EndY=-41.4 EndZ=0
    g1: LineSegment StartX=24.1 StartY=-41.4 StartZ=0 EndX=24.1 EndY=-39.4 EndZ=0
    g2: LineSegment StartX=24.1 StartY=-39.4 StartZ=0 EndX=11.9 EndY=-39.4 EndZ=0
    g3: LineSegment StartX=11.9 StartY=-39.4 StartZ=0 EndX=11.9 EndY=-41.4 EndZ=0
  constraints (10):
    c: Coincident(g0,g1)
    c: Coincident(g1,g2)
    c: Coincident(g2,g3)
    c: Coincident(g3,g0)
    c: Horizontal(g2)
    c: Vertical(g1)
    c: Vertical(g3)
    c: DistanceY(g1,g1) = 2
    c: Coincident(g0,g-7)
    c: Coincident(g0,g-6)
FEATURE [PartDesign::Pad] Pad004
  BaseFeature = -> Fillet
  Direction = (0,0,-1)
  Length = 1
  Length2 = 10
  Profile = -> Sketch012
  ReferenceAxis = -> Sketch012 [N_Axis]
  Refine = true
  Suppressed = false
  Type = 0
FEATURE [Sketcher::SketchObject] Sketch013
  ArcFitTolerance = 1e-06
  AttachmentSupport = -> [Pad004]
  ExternalGeometry = -> [Pad004]
  FullyConstrained = true
  MakeInternals = false
  MapMode = 5
  Placement = pos=(0,0,0) rot=(1,0,0;3.14159rad)
  sketch-geometry (16):
    g0: LineSegment StartX=9 StartY=-41.4 StartZ=0 EndX=9 EndY=-38.4 EndZ=0
    g1: LineSegment StartX=9 StartY=-38.4 StartZ=0 EndX=13.75 EndY=-38.4 EndZ=0
    g2: ArcOfCircle CenterX=13.75 CenterY=-37.4 CenterZ=0 NormalX=0 NormalY=0 NormalZ=1 AngleXU=0 Radius=1 StartAngle=4.71239 EndAngle=7.85398
    g3: LineSegment StartX=13.75 StartY=-36.4 StartZ=0 EndX=9 EndY=-36.4 EndZ=0
    g4: LineSegment StartX=9 StartY=-36.4 StartZ=0 EndX=9 EndY=-34.4 EndZ=0
    g5: LineSegment StartX=9 StartY=-34.4 StartZ=0 EndX=7 EndY=-34.4 EndZ=0
    g6: LineSegment StartX=7 StartY=-34.4 StartZ=0 EndX=7 EndY=-41.4 EndZ=0
    g7: LineSegment StartX=7 StartY=-41.4 StartZ=0 EndX=9 EndY=-41.4 EndZ=0
    g8: LineSegment StartX=27 StartY=-41.4 StartZ=0 EndX=29 EndY=-41.4 EndZ=0
    g9: LineSegment StartX=29 StartY=-41.4 StartZ=0 EndX=29 EndY=-34.4 EndZ=0
    g10: LineSegment StartX=29 StartY=-34.4 StartZ=0 EndX=27 EndY=-34.4 EndZ=0
    g11: LineSegment StartX=27 StartY=-34.4 StartZ=0 EndX=27 EndY=-36.4 EndZ=0
    g12: LineSegment StartX=27 StartY=-36.4 StartZ=0 EndX=22.25 EndY=-36.4 EndZ=0
    g13: LineSegment StartX=27 StartY=-41.4 StartZ=0 EndX=27 EndY=-38.4 EndZ=0
    g14: LineSegment StartX=27 StartY=-38.4 StartZ=0 EndX=22.25 EndY=-38.4 EndZ=0
    g15: ArcOfCircle CenterX=22.25 CenterY=-37.4 CenterZ=0 NormalX=0 NormalY=0 NormalZ=1 AngleXU=0 Radius=1 StartAngle=1.5708 EndAngle=4.71239
  constraints (51):
    c: PointOnObject(g0,g-4)
    c: Vertical(g0)
    c: Coincident(g1,g0)
    c: Horizontal(g1)
    c: Coincident(g2,g1)
    c: Coincident(g3,g2)
    c: Horizontal(g3)
    c: Coincident(g4,g3)
    c: Vertical(g4)
    c: Coincident(g5,g4)
    c: Horizontal(g5)
    c: Coincident(g6,g5)
    c: PointOnObject(g6,g-4)
    c: Coincident(g7,g6)
    c: Coincident(g7,g0)
    c: Vertical(g6)
    c: PointOnObject(g8,g-3)
    c: Coincident(g9,g8)
    c: Vertical(g9)
    c: Coincident(g10,g9)
    c: Horizontal(g10)
    c: Coincident(g11,g10)
    c: Coincident(g12,g11)
    c: Horizontal(g12)
    c: Coincident(g13,g8)
    c: Vertical(g13)
    c: Coincident(g14,g13)
    c: Horizontal(g14)
    c: Coincident(g15,g14)
    c: Coincident(g15,g12)
    c: Vertical(g11)
    c: DistanceX(g10,g10) = 2
    c: DistanceX(g8,g8) = 2
    c: DistanceX(g5,g5) = 2
    c: DistanceX(g7,g7) = 2
    c: DistanceY(g0,g3) = 2
    c: DistanceY(g13,g11) = 2
    c: DistanceY(g6,g6) = 7
    c: DistanceY(g9,g9) = 7
    c: DistanceX(g-5,g6) = 7
    c: DistanceX(g8,g-6) = 7
    c: DistanceX(g2,g15) = 8.5
    c: DistanceX(g15,g12) = 0
    c: DistanceX(g15,g14) = 0
    c: DistanceX(g2,g2) = 0
    c: DistanceX(g-7,g15) = 0.15
    c: DistanceY(g-9,g0) = 1
    c: DistanceY(g-9,g13) = 1
    c: DistanceX(g2,g1) = 0
    c: DistanceX(g2,g-8) = 0.15
    c: PointOnObject(g8,g-3)
FEATURE [PartDesign::Pad] Pad005
  BaseFeature = -> Pad004
  Direction = (0,0,-1)
  Length = 4
  Length2 = 10
  Profile = -> Sketch013
  ReferenceAxis = -> Sketch013 [N_Axis]
  Refine = true
  Suppressed = false
  Type = 0
FEATURE [Sketcher::SketchObject] Sketch014
  ArcFitTolerance = 1e-06
  AttachmentSupport = -> [Pad005]
  ExternalGeometry = -> [Pad005]
  FullyConstrained = true
  MakeInternals = false
  MapMode = 5
  Placement = pos=(0,0,-4) rot=(1,0,0;3.14159rad)
  sketch-geometry (2):
    g0: Circle CenterX=13.75 CenterY=-37.4 CenterZ=0 NormalX=0 NormalY=0 NormalZ=1 AngleXU=0 Radius=1
    g1: Circle CenterX=22.25 CenterY=-37.4 CenterZ=0 NormalX=0 NormalY=0 NormalZ=1 AngleXU=0 Radius=1
  constraints (4):
    c: Coincident(g0,g-4)
    c: Equal(g0,g-4)
    c: Coincident(g1,g-3)
    c: Equal(g1,g-3)
FEATURE [PartDesign::Pad] Pad006
  BaseFeature = -> Pad005
  Direction = (0,0,-1)
  Length = 2
  Length2 = 10
  Profile = -> Sketch014
  ReferenceAxis = -> Sketch014 [N_Axis]
  Refine = true
  Suppressed = false
  Type = 0
FEATURE [Sketcher::SketchObject] Sketch015
  ArcFitTolerance = 1e-06
  AttachmentSupport = -> [Pad006]
  ExternalGeometry = -> [Pad006]
  FullyConstrained = true
  MakeInternals = false
  MapMode = 5
  Placement = pos=(0,0,0) rot=(1,0,0;3.14159rad)
  sketch-geometry (14):
    g0: LineSegment StartX=29 StartY=-10.3 StartZ=0 EndX=29 EndY=-26.3 EndZ=0
    g1: LineSegment StartX=29 StartY=-26.3 StartZ=0 EndX=27 EndY=-26.3 EndZ=0
    g2: LineSegment StartX=27 StartY=-26.3 StartZ=0 EndX=27 EndY=-13.3 EndZ=0
    g3: LineSegment StartX=27 StartY=-13.3 StartZ=0 EndX=25.5 EndY=-13.3 EndZ=0
    g4: LineSegment StartX=25.5 StartY=-13.3 StartZ=0 EndX=25.5 EndY=-20.0303 EndZ=0
    g5: LineSegment StartX=25.5 StartY=-20.0303 StartZ=0 EndX=24 EndY=-24.8 EndZ=0
    g6: LineSegment StartX=24 StartY=-24.8 StartZ=0 EndX=12 EndY=-24.8 EndZ=0
    g7: LineSegment StartX=12 StartY=-24.8 StartZ=0 EndX=10.5 EndY=-20.0303 EndZ=0
    g8: LineSegment StartX=10.5 StartY=-20.0303 StartZ=0 EndX=10.5 EndY=-13.3 EndZ=0
    g9: LineSegment StartX=10.5 StartY=-13.3 StartZ=0 EndX=9 EndY=-13.3 EndZ=0
    g10: LineSegment StartX=9 StartY=-13.3 StartZ=0 EndX=9 EndY=-26.3 EndZ=0
    g11: LineSegment StartX=9 StartY=-26.3 StartZ=0 EndX=7 EndY=-26.3 EndZ=0
    g12: LineSegment StartX=7 StartY=-26.3 StartZ=0 EndX=7 EndY=-10.3 EndZ=0
    g13: LineSegment StartX=7 StartY=-10.3 StartZ=0 EndX=29 EndY=-10.3 EndZ=0
  constraints (43):
    c: PointOnObject(g0,g-4)
    c: Vertical(g0)
    c: Coincident(g1,g0)
    c: Horizontal(g1)
    c: Coincident(g2,g1)
    c: Vertical(g2)
    c: Coincident(g3,g2)
    c: Horizontal(g3)
    c: Coincident(g4,g3)
    c: Vertical(g4)
    c: Coincident(g5,g4)
    c: Coincident(g6,g5)
    c: Horizontal(g6)
    c: Coincident(g7,g6)
    c: Coincident(g8,g7)
    c: Vertical(g8)
    c: Coincident(g9,g8)
    c: Horizontal(g9)
    c: Coincident(g10,g9)
    c: Vertical(g10)
    c: Coincident(g11,g10)
    c: Horizontal(g11)
    c: Coincident(g12,g11)
    c: Vertical(g12)
    c: Coincident(g13,g12)
    c: Coincident(g13,g0)
    c: Horizontal(g13)
    c: DistanceX(g-8,g0) = 0
    c: DistanceX(g11,g-7) = 0
    c: DistanceX(g11,g11) = 2
    c: DistanceX(g1,g1) = 2
    c: DistanceX(g9,g9) = 1.5
    c: DistanceX(g3,g3) = 1.5
    c: DistanceY(g-7,g11) = 8.1
    c: DistanceY(g-8,g0) = 8.1
    c: DistanceX(g6,g6) = 12
    c: DistanceY(g10,g6) = 1.5
    c: DistanceY(g9,g12) = 3
    c: DistanceY(g2,g0) = 3
    c: DistanceX(g10,g1) = 18
    c: DistanceX(g10,g6) = 3
    c: Distance(g7) = 5
    c: Distance(g5) = 5
FEATURE [PartDesign::Pad] Pad007
  BaseFeature = -> Pad006
  Direction = (0,0,-1)
  Length = 4
  Length2 = 10
  Profile = -> Sketch015
  ReferenceAxis = -> Sketch015 [N_Axis]
  Refine = true
  Suppressed = false
  Type = 0
FEATURE [Sketcher::SketchObject] Sketch016
  ArcFitTolerance = 1e-06
  AttachmentSupport = -> [Pad007]
  ExternalGeometry = -> [Pad007]
  FullyConstrained = true
  MakeInternals = false
  MapMode = 5
  Placement = pos=(0,0,-4) rot=(1,0,0;3.14159rad)
  sketch-geometry (1):
    g0: Circle CenterX=18 CenterY=-20.4 CenterZ=0 NormalX=0 NormalY=0 NormalZ=1 AngleXU=0 Radius=2.4
  constraints (5):
    c: Diameter(g0) = 4.8
    c: DistanceY(g-4,g0) = 4.4
    c: DistanceX(g-4,g-4) = 12
    c: DistanceX(g-4,g-4) = 12
    c: DistanceX(g-4,g0) = 6
FEATURE [PartDesign::Pad] Pad008
  BaseFeature = -> Pad007
  Direction = (0,0,-1)
  Length = 2.5
  Length2 = 10
  Profile = -> Sketch016
  ReferenceAxis = -> Sketch016 [N_Axis]
  Refine = true
  Suppressed = false
  Type = 0
FEATURE [Sketcher::SketchObject] Sketch017
  ArcFitTolerance = 1e-06
  AttachmentSupport = -> [Pad008]
  ExternalGeometry = -> [Pad008]
  FullyConstrained = true
  MakeInternals = false
  MapMode = 5
  Placement = pos=(0,0,-6.5) rot=(1,0,0;3.14159rad)
  sketch-geometry (1):
    g0: Circle CenterX=18 CenterY=-20.4 CenterZ=0 NormalX=0 NormalY=0 NormalZ=1 AngleXU=0 Radius=0.75
  constraints (2):
    c: Coincident(g0,g-3)
    c: Diameter(g0) = 1.5
FEATURE [PartDesign::Pocket] Pocket008
  BaseFeature = -> Pad008
  Direction = (0,0,1)
  Length = 7
  Length2 = 5
  Profile = -> Sketch017
  ReferenceAxis = -> Sketch017 [N_Axis]
  Refine = true
  Suppressed = false
  Type = 0
FEATURE [Sketcher::SketchObject] Sketch018
  ArcFitTolerance = 1e-06
  AttachmentSupport = -> [Pocket008]
  ExternalGeometry = -> [Pocket008]
  FullyConstrained = true
  MakeInternals = false
  MapMode = 5
  Placement = pos=(0,0,0) rot=(1,0,0;3.14159rad)
  sketch-geometry (4):
    g0: LineSegment StartX=0 StartY=0 StartZ=0 EndX=0 EndY=-10.3 EndZ=0
    g1: LineSegment StartX=0 StartY=-10.3 StartZ=0 EndX=9 EndY=-10.3 EndZ=0
    g2: LineSegment StartX=9 StartY=-10.3 StartZ=0 EndX=9 EndY=0 EndZ=0
    g3: LineSegment StartX=9 StartY=0 StartZ=0 EndX=0 EndY=0 EndZ=0
  constraints (11):
    c: Coincident(g0,g1)
    c: Coincident(g1,g2)
    c: Coincident(g2,g3)
    c: Coincident(g3,g0)
    c: Vertical(g0)
    c: Vertical(g2)
    c: Horizontal(g1)
    c: Horizontal(g3)
    c: Coincident(g0,g-1)
    c: PointOnObject(g1,g-4)
    c: DistanceX(g-5,g1) = 1
FEATURE [PartDesign::Pad] Pad009
  BaseFeature = -> Pocket008
  Direction = (0,0,-1)
  Length = 2
  Length2 = 10
  Profile = -> Sketch018
  ReferenceAxis = -> Sketch018 [N_Axis]
  Refine = true
  Suppressed = false
  Type = 0
FEATURE [Sketcher::SketchObject] Sketch019
  ArcFitTolerance = 1e-06
  AttachmentSupport = -> [Pad009]
  ExternalGeometry = -> [Pad009]
  FullyConstrained = true
  MakeInternals = false
  MapMode = 5
  Placement = pos=(0,0,-4) rot=(1,0,0;3.14159rad)
  sketch-geometry (4):
    g0: LineSegment StartX=7 StartY=-10.3 StartZ=0 EndX=29 EndY=-10.3 EndZ=0
    g1: LineSegment StartX=29 StartY=-10.3 StartZ=0 EndX=29 EndY=0 EndZ=0
    g2: LineSegment StartX=29 StartY=0 StartZ=0 EndX=7 EndY=0 EndZ=0
    g3: LineSegment StartX=7 StartY=0 StartZ=0 EndX=7 EndY=-10.3 EndZ=0
  constraints (10):
    c: Coincident(g0,g1)
    c: Coincident(g1,g2)
    c: Coincident(g2,g3)
    c: Coincident(g3,g0)
    c: Horizontal(g2)
    c: Vertical(g1)
    c: Vertical(g3)
    c: Coincident(g0,g-3)
    c: PointOnObject(g1,g-1)
    c: Coincident(g0,g-3)
FEATURE [PartDesign::Pad] Pad010
  BaseFeature = -> Pad009
  Direction = (0,0,-1)
  Length = 2
  Length2 = 10
  Profile = -> Sketch019
  ReferenceAxis = -> Sketch019 [N_Axis]
  Refine = true
  Reversed = true
  Suppressed = false
  Type = 0
FEATURE [PartDesign::Body] Body  label="Rear_Torso"
  AllowCompound = false
  Group = -> [Sketch,Pad,Sketch001,Pocket,Sketch002,Pocket001,Sketch003,Pocket002,LinearPattern,Sketch004,Pocket003,Sketch005,Pocket004,LinearPattern001,Sketch006,Pad001,Sketch007,Pocket005,Sketch008,Pocket006,Sketch009,Pad002,Sketch010,Pocket007,Sketch011,Pad003,Fillet,Sketch012,Pad004,Sketch013,Pad005,Sketch014,Pad006,Sketch015,Pad007,Sketch016,Pad008,Sketch017,Pocket008,Sketch018,Pad009,Sketch019,Pad010,+20 more]
  Origin = -> Origin
  Tip = -> Pocket040
COMPONENT P1 — recipe-attached ("Inner_Crane_Boom", modeled in this document).
Construction recipe (the document's own serialized feature program — sketch geometry with constraints, then the solid features built on it; lengths are millimeters unless a unit is written):

FEATURE [Sketcher::SketchObject] Sketch028
  ArcFitTolerance = 1e-06
  AttachmentSupport = -> [XY_Plane001]
  FullyConstrained = true
  MakeInternals = false
  MapMode = 5
  sketch-geometry (4):
    g0: LineSegment StartX=0 StartY=0 StartZ=0 EndX=63.3 EndY=0 EndZ=0
    g1: LineSegment StartX=63.3 StartY=0 StartZ=0 EndX=63.3 EndY=4 EndZ=0
    g2: LineSegment StartX=63.3 StartY=4 StartZ=0 EndX=0 EndY=4 EndZ=0
    g3: LineSegment StartX=0 StartY=4 StartZ=0 EndX=0 EndY=0 EndZ=0
  constraints (11):
    c: Coincident(g0,g1)
    c: Coincident(g1,g2)
    c: Coincident(g2,g3)
    c: Coincident(g3,g0)
    c: Horizontal(g0)
    c: Horizontal(g2)
    c: Vertical(g1)
    c: Vertical(g3)
    c: Coincident(g0,g-1)
    c: DistanceX(g2,g2) = 63.3
    c: DistanceY(g1,g1) = 4
FEATURE [PartDesign::Pad] Pad015
  Direction = (0,0,1)
  Length = 2.75
  Length2 = 10
  Profile = -> Sketch028
  ReferenceAxis = -> Sketch028 [N_Axis]
  Refine = true
  Suppressed = false
  Type = 0
FEATURE [Sketcher::SketchObject] Sketch029
  ArcFitTolerance = 1e-06
  AttachmentSupport = -> [Pad015]
  ExternalGeometry = -> [Pad015]
  FullyConstrained = true
  MakeInternals = false
  MapMode = 5
  Placement = pos=(0,0,2.75) rot=(0,0,1;0rad)
  sketch-geometry (4):
    g0: LineSegment StartX=63.3 StartY=4 StartZ=0 EndX=63.3 EndY=5 EndZ=0
    g1: LineSegment StartX=63.3 StartY=5 StartZ=0 EndX=58.3 EndY=5 EndZ=0
    g2: LineSegment StartX=58.3 StartY=5 StartZ=0 EndX=58.3 EndY=4 EndZ=0
    g3: LineSegment StartX=58.3 StartY=4 StartZ=0 EndX=63.3 EndY=4 EndZ=0
  constraints (11):
    c: Coincident(g0,g1)
    c: Coincident(g1,g2)
    c: Coincident(g2,g3)
    c: Coincident(g3,g0)
    c: Vertical(g0)
    c: Vertical(g2)
    c: Horizontal(g1)
    c: Horizontal(g3)
    c: Coincident(g0,g-3)
    c: DistanceX(g1,g1) = 5
    c: DistanceY(g2,g2) = 1
FEATURE [PartDesign::Pad] Pad016
  BaseFeature = -> Pad015
  Direction = (0,0,1)
  Length = 2.75
  Length2 = 10
  Profile = -> Sketch029
  ReferenceAxis = -> Sketch029 [N_Axis]
  Refine = true
  Reversed = true
  Suppressed = false
  Type = 0
FEATURE [Sketcher::SketchObject] Sketch030
  ArcFitTolerance = 1e-06
  AttachmentOffset = pos=(0,0,1.125) rot=(0,0,1;0rad)
  AttachmentSupport = -> [Pad016]
  ExternalGeometry = -> [Pad016]
  FullyConstrained = true
  MakeInternals = false
  MapMode = 5
  Placement = pos=(0,0,3.875) rot=(0,0,1;0rad)
  sketch-geometry (6):
    g0: LineSegment StartX=0 StartY=4 StartZ=0 EndX=-2 EndY=10.7 EndZ=0
    g1: LineSegment StartX=-2 StartY=10.7 StartZ=0 EndX=-7 EndY=10.7 EndZ=0
    g2: LineSegment StartX=-7 StartY=10.7 StartZ=0 EndX=-7 EndY=-4.3 EndZ=0
    g3: LineSegment StartX=-7 StartY=-4.3 StartZ=0 EndX=-2 EndY=-4.3 EndZ=0
    g4: LineSegment StartX=-2 StartY=-4.3 StartZ=0 EndX=0 EndY=0 EndZ=0
    g5: LineSegment StartX=0 StartY=4 StartZ=0 EndX=0 EndY=0 EndZ=0
  constraints (16):
    c: Coincident(g1,g0)
    c: Horizontal(g1)
    c: Coincident(g2,g1)
    c: Vertical(g2)
    c: Coincident(g3,g2)
    c: Horizontal(g3)
    c: Coincident(g4,g3)
    c: Coincident(g4,g-1)
    c: Coincident(g5,g0)
    c: Coincident(g5,g4)
    c: DistanceX(g2,g4) = 7
    c: DistanceY(g2,g2) = 15
    c: DistanceX(g1,g1) = 5
    c: DistanceX(g3,g3) = 5
    c: DistanceY(g3,g4) = 4.3
    c: Coincident(g0,g-3)
FEATURE [PartDesign::Pad] Pad017
  BaseFeature = -> Pad016
  Direction = (0,0,1)
  Length = 5
  Length2 = 10
  Profile = -> Sketch030
  ReferenceAxis = -> Sketch030 [N_Axis]
  Refine = true
  Reversed = true
  Suppressed = false
  Type = 0
FEATURE [Sketcher::SketchObject] Sketch031
  ArcFitTolerance = 1e-06
  AttachmentSupport = -> [Pad017]
  ExternalGeometry = -> [Pad017]
  FullyConstrained = true
  MakeInternals = false
  MapMode = 5
  Placement = pos=(0,0,0) rot=(1,0,0;1.5708rad)
  sketch-geometry (6):
    g0: LineSegment StartX=0 StartY=3.875 StartZ=0 EndX=0 EndY=2.75 EndZ=0
    g1: LineSegment StartX=0 StartY=2.75 StartZ=0 EndX=4 EndY=2.75 EndZ=0
    g2: LineSegment StartX=4 StartY=2.75 StartZ=0 EndX=0 EndY=3.875 EndZ=0
    g3: LineSegment StartX=0 StartY=0 StartZ=0 EndX=0 EndY=-1.125 EndZ=0
    g4: LineSegment StartX=0 StartY=-1.125 StartZ=0 EndX=4 EndY=0 EndZ=0
    g5: LineSegment StartX=4 StartY=0 StartZ=0 EndX=0 EndY=0 EndZ=0
  constraints (14):
    c: Coincident(g0,g-4)
    c: Coincident(g0,g-4)
    c: Coincident(g1,g0)
    c: PointOnObject(g1,g-3)
    c: Coincident(g2,g1)
    c: Coincident(g2,g0)
    c: Coincident(g3,g-1)
    c: Coincident(g3,g-6)
    c: Coincident(g4,g3)
    c: PointOnObject(g4,g-5)
    c: Coincident(g5,g4)
    c: Coincident(g5,g3)
    c: DistanceX(g1,g1) = 4
    c: DistanceX(g5,g5) = 4
FEATURE [PartDesign::Pad] Pad018
  BaseFeature = -> Pad017
  Direction = (0,-1,2e-16)
  Length = 4
  Length2 = 10
  Profile = -> Sketch031
  ReferenceAxis = -> Sketch031 [N_Axis]
  Refine = true
  Reversed = true
  Suppressed = false
  Type = 0
FEATURE [Sketcher::SketchObject] Sketch032
  ArcFitTolerance = 1e-06
  AttachmentSupport = -> [Pad018]
  ExternalGeometry = -> [Pad018]
  FullyConstrained = true
  MakeInternals = false
  MapMode = 5
  Placement = pos=(0,-4.3,0) rot=(1,0,0;1.5708rad)
  sketch-geometry (4):
    g0: LineSegment StartX=-7 StartY=2.375 StartZ=0 EndX=-7 EndY=0.375 EndZ=0
    g1: LineSegment StartX=-7 StartY=0.375 StartZ=0 EndX=0 EndY=0.375 EndZ=0
    g2: LineSegment StartX=0 StartY=0.375 StartZ=0 EndX=0 EndY=2.375 EndZ=0
    g3: LineSegment StartX=0 StartY=2.375 StartZ=0 EndX=-7 EndY=2.375 EndZ=0
  constraints (12):
    c: Coincident(g0,g1)
    c: Coincident(g1,g2)
    c: Coincident(g2,g3)
    c: Coincident(g3,g0)
    c: Vertical(g0)
    c: Vertical(g2)
    c: Horizontal(g1)
    c: Horizontal(g3)
    c: PointOnObject(g0,g-3)
    c: DistanceY(g0,g0) = 2
    c: DistanceY(g0,g-3) = 1.5
    c: PointOnObject(g2,g-2)
FEATURE [PartDesign::Pocket] Pocket014
  BaseFeature = -> Pad018
  Direction = (0,1,-2e-16)
  Length = 15
  Length2 = 5
  Profile = -> Sketch032
  ReferenceAxis = -> Sketch032 [N_Axis]
  Refine = true
  Suppressed = false
  Type = 0
FEATURE [Sketcher::SketchObject] Sketch033
  ArcFitTolerance = 1e-06
  AttachmentSupport = -> [Pocket014]
  ExternalGeometry = -> [Pocket014]
  FullyConstrained = true
  MakeInternals = false
  MapMode = 5
  Placement = pos=(0,0,3.875) rot=(0,0,1;0rad)
  sketch-geometry (2):
    g0: Circle CenterX=-3.5 CenterY=-1 CenterZ=0 NormalX=0 NormalY=0 NormalZ=1 AngleXU=0 Radius=0.8
    g1: Circle CenterX=-3.5 CenterY=9.2 CenterZ=0 NormalX=0 NormalY=0 NormalZ=1 AngleXU=0 Radius=0.8
  constraints (6):
    c: Diameter(g0) = 1.6
    c: Diameter(g1) = 1.6
    c: DistanceX(g1,g0) = 0
    c: DistanceY(g1,g-3) = 1.5
    c: DistanceX(g1,g-3) = 1.5
    c: DistanceY(g0,g-1) = 1
FEATURE [PartDesign::Pad] Pad019
  BaseFeature = -> Pocket014
  Direction = (0,0,1)
  Length = 0.5
  Length2 = 10
  Profile = -> Sketch033
  ReferenceAxis = -> Sketch033 [N_Axis]
  Refine = true
  Suppressed = false
  Type = 0
FEATURE [Sketcher::SketchObject] Sketch034
  ArcFitTolerance = 1e-06
  AttachmentSupport = -> [Pad019]
  ExternalGeometry = -> [Pad019]
  FullyConstrained = true
  MakeInternals = false
  MapMode = 5
  Placement = pos=(0,0,3.875) rot=(0,0,1;0rad)
  sketch-geometry (1):
    g0: Circle CenterX=-3.5 CenterY=5 CenterZ=0 NormalX=0 NormalY=0 NormalZ=1 AngleXU=0 Radius=1
  constraints (4):
    c: Diameter(g0) = 2
    c: DistanceY(g-3,g0) = 1
    c: DistanceX(g-4,g-3) = 7
    c: DistanceX(g0,g-3) = 3.5
FEATURE [PartDesign::Pocket] Pocket015
  BaseFeature = -> Pad019
  Direction = (0,0,-1)
  Length = 5
  Length2 = 5
  Profile = -> Sketch034
  ReferenceAxis = -> Sketch034 [N_Axis]
  Refine = true
  Suppressed = false
  Type = 0
FEATURE [Sketcher::SketchObject] Sketch035
  ArcFitTolerance = 1e-06
  AttachmentSupport = -> [Pocket015]
  ExternalGeometry = -> [Pocket015]
  FullyConstrained = true
  MakeInternals = false
  MapMode = 5
  Placement = pos=(0,0,-1.125) rot=(1,0,0;3.14159rad)
  sketch-geometry (2):
    g0: Circle CenterX=-3.5 CenterY=1 CenterZ=0 NormalX=0 NormalY=0 NormalZ=1 AngleXU=0 Radius=0.8
    g1: Circle CenterX=-3.5 CenterY=-9.2 CenterZ=0 NormalX=0 NormalY=0 NormalZ=1 AngleXU=0 Radius=0.8
  constraints (6):
    c: Diameter(g0) = 1.6
    c: Diameter(g1) = 1.6
    c: DistanceX(g0,g1) = 0
    c: DistanceY(g-1,g0) = 1
    c: DistanceX(g1,g-3) = 1.5
    c: DistanceY(g-3,g1) = 1.5
FEATURE [PartDesign::Pad] Pad020
  BaseFeature = -> Pocket015
  Direction = (0,0,-1)
  Length = 0.5
  Length2 = 10
  Profile = -> Sketch035
  ReferenceAxis = -> Sketch035 [N_Axis]
  Refine = true
  Suppressed = false
  Type = 0
FEATURE [PartDesign::Pocket] Pocket023
  BaseFeature = -> Pad020
  Direction = (0,-1,0)
  Length = 0.1
  Length2 = 5
  Profile = -> Pad020 [Face25]
  Refine = true
  Suppressed = false
  Type = 0
FEATURE [Sketcher::SketchObject] Sketch340
  ArcFitTolerance = 1e-06
  AttachmentSupport = -> [Pocket023]
  ExternalGeometry = -> [Pocket023]
  FullyConstrained = true
  MakeInternals = false
  MapMode = 5
  Placement = pos=(0,0,0) rot=(1,0,0;3.14159rad)
  sketch-geometry (3):
    g0: LineSegment StartX=58.3 StartY=-4 StartZ=0 EndX=56.3 EndY=-4 EndZ=0
    g1: LineSegment StartX=56.3 StartY=-4 StartZ=0 EndX=58.3 EndY=-4.25 EndZ=0
    g2: LineSegment StartX=58.3 StartY=-4.25 StartZ=0 EndX=58.3 EndY=-4 EndZ=0
  constraints (8):
    c: Coincident(g0,g-4)
    c: PointOnObject(g0,g-4)
    c: Coincident(g1,g0)
    c: PointOnObject(g1,g-3)
    c: Coincident(g2,g1)
    c: Coincident(g2,g0)
    c: DistanceY(g2,g2) = 0.25
    c: DistanceX(g0,g0) = 2
FEATURE [PartDesign::Pad] Pad241
  BaseFeature = -> Pocket023
  Direction = (0,0,-1)
  Length = 2.75
  Length2 = 10
  Profile = -> Sketch340
  ReferenceAxis = -> Sketch340 [N_Axis]
  Refine = true
  Reversed = true
  Suppressed = false
  Type = 0
FEATURE [PartDesign::Body] Body001  label="Inner_Crane_Boom"
  AllowCompound = false
  Group = -> [Sketch028,Pad015,Sketch029,Pad016,Sketch030,Pad017,Sketch031,Pad018,Sketch032,Pocket014,Sketch033,Pad019,Sketch034,Pocket015,Sketch035,Pad020,Pocket023,Sketch340,Pad241]
  Origin = -> Origin001
  Placement = pos=(19.43,-36.85,26.85) rot=(0.57735,0.57735,-0.57735;4.18879rad)
  Tip = -> Pad241
COMPONENT P2 — recipe-attached ("Outer_Left_Crane_Boom", modeled in this document).
Construction recipe (the document's own serialized feature program — sketch geometry with constraints, then the solid features built on it; lengths are millimeters unless a unit is written):

FEATURE [PartDesign::SubShapeBinder] Binder
  BindCopyOnChange = 0
  BindMode = 2
  ClaimChildren = false
  Context = -> Body002 [Binder.]
  Fuse = false
  MakeFace = true
  OffsetFill = false
  OffsetIntersection = false
  OffsetJoinType = 0
  OffsetOpenResult = false
  PartialLoad = false
  Refine = true
  Relative = true
  _Version = 2
FEATURE [Sketcher::SketchObject] Sketch036
  ArcFitTolerance = 1e-06
  AttachmentSupport = -> [Binder]
  ExternalGeometry = -> [Binder]
  FullyConstrained = true
  MakeInternals = false
  MapMode = 5
  Placement = pos=(0,0,2.75) rot=(0,0,1;0rad)
  sketch-geometry (18):
    g0: LineSegment StartX=16.4156 StartY=-2.05 StartZ=0 EndX=83.023 EndY=-2.05 EndZ=0
    g1: LineSegment StartX=83.023 StartY=-2.05 StartZ=0 EndX=78.7784 EndY=13.7912 EndZ=0
    g2: ArcOfCircle CenterX=75.717 CenterY=12.7 CenterZ=0 NormalX=0 NormalY=0 NormalZ=1 AngleXU=0 Radius=3.25 StartAngle=0.3424 EndAngle=2.94413
    g3: LineSegment StartX=72.5302 StartY=13.3376 StartZ=0 EndX=71.2452 EndY=6.05 EndZ=0
    g4: LineSegment StartX=71.2452 StartY=6.05 StartZ=0 EndX=14.2452 EndY=6.05 EndZ=0
    g5: LineSegment StartX=14.2452 StartY=6.05 StartZ=0 EndX=14.004 EndY=6.95 EndZ=0
    g6: LineSegment StartX=14.004 StartY=6.95 StartZ=0 EndX=9.42121 EndY=6.95 EndZ=0
    g7: LineSegment StartX=9.42121 StartY=6.95 StartZ=0 EndX=9.13277 EndY=8.02646 EndZ=0
    g8: ArcOfCircle CenterX=6.23499 CenterY=7.25 CenterZ=0 NormalX=0 NormalY=0 NormalZ=1 AngleXU=0 Radius=3 StartAngle=0.261799 EndAngle=3.40339
    g9: LineSegment StartX=3.33722 StartY=6.47354 StartZ=0 EndX=6.02302 EndY=-3.55 EndZ=0
    g10: LineSegment StartX=16.6835 StartY=-3.05 StartZ=0 EndX=16.4156 EndY=-2.05 EndZ=0
    g11: LineSegment StartX=6.02302 StartY=-3.55 StartZ=0 EndX=12.2347 EndY=-3.55 EndZ=0
    g12: LineSegment StartX=12.2347 StartY=-3.55 StartZ=0 EndX=12.1007 EndY=-3.05 EndZ=0
    g13: LineSegment StartX=12.1007 StartY=-3.05 StartZ=0 EndX=16.6835 EndY=-3.05 EndZ=0
    g14: LineSegment [constr] StartX=14.2452 StartY=6.05 StartZ=0 EndX=16.4156 EndY=-2.05 EndZ=0
    g15: LineSegment [constr] StartX=9.42121 StartY=6.95 StartZ=0 EndX=12.1007 EndY=-3.05 EndZ=0
    g16: LineSegment [constr] StartX=6.23499 StartY=7.25 StartZ=0 EndX=3.33722 EndY=6.47354 EndZ=0
    g17: LineSegment [constr] StartX=6.23499 StartY=7.25 StartZ=0 EndX=9.13277 EndY=8.02646 EndZ=0
  constraints (53):
    c: Horizontal(g0)
    c: Coincident(g1,g0)
    c: Coincident(g2,g1)
    c: Coincident(g3,g2)
    c: Coincident(g4,g3)
    c: Horizontal(g4)
    c: Coincident(g5,g4)
    c: Coincident(g6,g5)
    c: Horizontal(g6)
    c: Coincident(g7,g6)
    c: Coincident(g8,g7)
    c: Coincident(g9,g8)
    c: Coincident(g10,g0)
    c: Coincident(g11,g9)
    c: Horizontal(g11)
    c: Coincident(g12,g11)
    c: Coincident(g13,g12)
    c: Coincident(g13,g10)
    c: Horizontal(g13)
    c: DistanceX(g9,g0) = 77
    c: DistanceY(g0,g4) = 8.1
    c: Diameter(g2) = 6.5
    c: Diameter(g8) = 6
    c: DistanceX(g4,g4) = 57
    c: DistanceY(g0,g2) = 14.75
    c: Angle(g1,g0) = 1.309
    c: Angle(g3,g1) = 0.436332
    c: Distance(g1) = 16.4
    c: Distance(g3) = 7.4
    c: Coincident(g14,g4)
    c: Coincident(g14,g0)
    c: Coincident(g15,g6)
    c: Coincident(g15,g12)
    c: Parallel(g7,g15)
    c: Parallel(g5,g14)
    c: Parallel(g10,g14)
    c: Parallel(g12,g15)
    c: Parallel(g15,g14)
    c: Parallel(g15,g9)
    c: Parallel(g1,g14)
    c: DistanceY(g-3,g-3) = 4
    c: DistanceY(g-3,g4) = 2.05
    c: DistanceY(g12,g5) = 10
    c: DistanceY(g10,g0) = 1
    c: DistanceY(g11,g12) = 0.5
    c: Coincident(g16,g8)
    c: Coincident(g16,g8)
    c: Coincident(g17,g8)
    c: Coincident(g17,g7)
    c: Angle(g16,g17) = 3.14159
    c: Angle(g17,g7) = 1.5708
    c: PointOnObject(g-3,g9)
    c: DistanceY(g9,g8) = 10.8
FEATURE [PartDesign::Pad] Pad021
  Direction = (0,0,1)
  Length = 1.5
  Length2 = 10
  Profile = -> Sketch036
  ReferenceAxis = -> Sketch036 [N_Axis]
  Refine = true
  Suppressed = false
  Type = 0
FEATURE [Sketcher::SketchObject] Sketch037
  ArcFitTolerance = 1e-06
  AttachmentSupport = -> [Pad021]
  ExternalGeometry = -> [Pad021]
  FullyConstrained = true
  MakeInternals = false
  MapMode = 5
  Placement = pos=(0,0,4.25) rot=(0,0,1;0rad)
  sketch-geometry (12):
    g0: LineSegment StartX=14.004 StartY=6.95 StartZ=0 EndX=16.6835 EndY=-3.05 EndZ=0
    g1: LineSegment StartX=16.6835 StartY=-3.05 StartZ=0 EndX=12.1007 EndY=-3.05 EndZ=0
    g2: LineSegment StartX=12.1007 StartY=-3.05 StartZ=0 EndX=12.2347 EndY=-3.55 EndZ=0
    g3: LineSegment StartX=12.2347 StartY=-3.55 StartZ=0 EndX=6.02302 EndY=-3.55 EndZ=0
    g4: LineSegment StartX=6.02302 StartY=-3.55 StartZ=0 EndX=3.33722 EndY=6.47354 EndZ=0
    g5: LineSegment StartX=14.004 StartY=6.95 StartZ=0 EndX=9.42121 EndY=6.95 EndZ=0
    g6: LineSegment StartX=9.42121 StartY=6.95 StartZ=0 EndX=9.13277 EndY=8.02646 EndZ=0
    g7: ArcOfCircle CenterX=6.23499 CenterY=7.25 CenterZ=0 NormalX=0 NormalY=0 NormalZ=1 AngleXU=0 Radius=3 StartAngle=0.261799 EndAngle=3.40339
    g8: LineSegment StartX=72.5302 StartY=13.3376 StartZ=0 EndX=69.8169 EndY=-2.05 EndZ=0
    g9: LineSegment StartX=78.7784 StartY=13.7912 StartZ=0 EndX=83.023 EndY=-2.05 EndZ=0
    g10: LineSegment StartX=83.023 StartY=-2.05 StartZ=0 EndX=69.8169 EndY=-2.05 EndZ=0
    g11: ArcOfCircle CenterX=75.717 CenterY=12.7 CenterZ=0 NormalX=0 NormalY=0 NormalZ=1 AngleXU=0 Radius=3.25 StartAngle=0.342399 EndAngle=2.94414
  constraints (27):
    c: Coincident(g0,g-7)
    c: Coincident(g0,g-10)
    c: Coincident(g1,g0)
    c: Coincident(g1,g-11)
    c: Coincident(g2,g1)
    c: Coincident(g2,g-11)
    c: Coincident(g3,g2)
    c: Coincident(g3,g-5)
    c: Coincident(g4,g3)
    c: Coincident(g4,g-4)
    c: Coincident(g5,g0)
    c: Coincident(g5,g-8)
    c: Coincident(g6,g5)
    c: Coincident(g6,g-8)
    c: Coincident(g7,g4)
    c: Coincident(g7,g6)
    c: Tangent(g7,g-3)
    c: Coincident(g8,g-14)
    c: PointOnObject(g8,g-15)
    c: Coincident(g9,g-14)
    c: Coincident(g9,g-15)
    c: Coincident(g10,g9)
    c: Coincident(g10,g8)
    c: PointOnObject(g-13,g8)
    c: Coincident(g11,g8)
    c: Coincident(g11,g9)
    c: Tangent(g11,g-14)
FEATURE [PartDesign::Pad] Pad022
  BaseFeature = -> Pad021
  Direction = (0,0,1)
  Length = 1
  Length2 = 10
  Profile = -> Sketch037
  ReferenceAxis = -> Sketch037 [N_Axis]
  Refine = true
  Suppressed = false
  Type = 0
FEATURE [PartDesign::Pad] Pad023
  BaseFeature = -> Pad022
  Direction = (0,0,1)
  Length = 1
  Length2 = 10
  Profile = -> Sketch037
  ReferenceAxis = -> Sketch037 [N_Axis]
  Refine = true
  Suppressed = false
  Type = 0
FEATURE [Sketcher::SketchObject] Sketch038
  ArcFitTolerance = 1e-06
  AttachmentSupport = -> [Pad023]
  ExternalGeometry = -> [Pad023]
  FullyConstrained = true
  MakeInternals = false
  MapMode = 5
  Placement = pos=(0,0,4.25) rot=(0,0,1;0rad)
  sketch-geometry (4):
    g0: LineSegment StartX=70.2452 StartY=6.05 StartZ=0 EndX=68.8169 EndY=-2.05 EndZ=0
    g1: LineSegment StartX=69.8169 StartY=-2.05 StartZ=0 EndX=68.8169 EndY=-2.05 EndZ=0
    g2: LineSegment StartX=69.8169 StartY=-2.05 StartZ=0 EndX=71.2452 EndY=6.05 EndZ=0
    g3: LineSegment StartX=70.2452 StartY=6.05 StartZ=0 EndX=71.2452 EndY=6.05 EndZ=0
  constraints (10):
    c: PointOnObject(g0,g-4)
    c: PointOnObject(g0,g-5)
    c: Coincident(g1,g-5)
    c: Coincident(g1,g0)
    c: Coincident(g2,g1)
    c: Coincident(g2,g-4)
    c: Coincident(g3,g0)
    c: Coincident(g3,g2)
    c: DistanceX(g3,g3) = 1
    c: DistanceX(g1,g1) = 1
FEATURE [PartDesign::Pad] Pad024
  BaseFeature = -> Pad023
  Direction = (0,0,1)
  Length = 1
  Length2 = 10
  Profile = -> Sketch038
  ReferenceAxis = -> Sketch038 [N_Axis]
  Refine = true
  Suppressed = false
  Type = 0
FEATURE [PartDesign::Chamfer] Chamfer
  Angle = 45
  Base = -> Pad024 [Edge52]
  BaseFeature = -> Pad024
  ChamferType = 0
  FlipDirection = false
  Refine = true
  Size = 0.99
  Size2 = 1
  SupportTransform = false
  Suppressed = false
  UseAllEdges = false
FEATURE [Sketcher::SketchObject] Sketch039
  ArcFitTolerance = 1e-06
  AttachmentSupport = -> [Chamfer]
  ExternalGeometry = -> [Chamfer,Binder]
  FullyConstrained = true
  MakeInternals = false
  MapMode = 5
  Placement = pos=(0,0,2.75) rot=(1,0,0;3.14159rad)
  sketch-geometry (28):
    g0: LineSegment StartX=71.2452 StartY=-6.05 StartZ=0 EndX=14.2452 EndY=-6.05 EndZ=0
    g1: LineSegment StartX=14.2452 StartY=-6.05 StartZ=0 EndX=14.004 EndY=-6.95 EndZ=0
    g2: LineSegment StartX=14.004 StartY=-6.95 StartZ=0 EndX=9.42121 EndY=-6.95 EndZ=0
    g3: LineSegment StartX=9.42121 StartY=-6.95 StartZ=0 EndX=9.13277 EndY=-8.02646 EndZ=0
    g4: LineSegment StartX=72.5038 StartY=-4.55 StartZ=0 EndX=10.6206 EndY=-4.55 EndZ=0
    g5: LineSegment StartX=81.0134 StartY=0.55 StartZ=0 EndX=5.21917 EndY=0.55 EndZ=0
    g6: LineSegment StartX=72.5038 StartY=-4.55 StartZ=0 EndX=74.0014 EndY=-13.0432 EndZ=0
    g7: ArcOfCircle CenterX=75.717 CenterY=-12.7 CenterZ=0 NormalX=0 NormalY=0 NormalZ=1 AngleXU=0 Radius=1.74961 StartAngle=3.33905 EndAngle=5.75206
    g8: LineSegment StartX=77.2256 StartY=-13.5862 StartZ=0 EndX=81.0134 EndY=0.55 EndZ=0
    g9: LineSegment [constr] StartX=79.9781 StartY=-3.3137 StartZ=0 EndX=81.4781 EndY=-3.71563 EndZ=0
    g10: LineSegment StartX=5.21917 StartY=0.55 StartZ=0 EndX=6.02302 EndY=3.55 EndZ=0
    g11: LineSegment StartX=83.023 StartY=2.05 StartZ=0 EndX=16.4156 EndY=2.05 EndZ=0
    g12: LineSegment StartX=16.4156 StartY=2.05 StartZ=0 EndX=16.6835 EndY=3.05 EndZ=0
    g13: LineSegment StartX=16.6835 StartY=3.05 StartZ=0 EndX=12.1007 EndY=3.05 EndZ=0
    g14: LineSegment StartX=12.1007 StartY=3.05 StartZ=0 EndX=12.2347 EndY=3.55 EndZ=0
    g15: LineSegment StartX=12.2347 StartY=3.55 StartZ=0 EndX=6.02302 EndY=3.55 EndZ=0
    g16: LineSegment StartX=6.02302 StartY=3.55 StartZ=0 EndX=5.21917 EndY=0.55 EndZ=0
    g17: LineSegment [constr] StartX=73.1565 StartY=-8.25155 StartZ=0 EndX=71.6793 EndY=-8.51202 EndZ=0
    g18: LineSegment [constr] StartX=72.5302 StartY=-13.3376 StartZ=0 EndX=74.0014 EndY=-13.0432 EndZ=0
    g19: LineSegment [constr] StartX=74.0014 StartY=-13.0432 StartZ=0 EndX=75.717 EndY=-12.7 EndZ=0
    g20: LineSegment StartX=10.6206 StartY=-4.55 StartZ=0 EndX=10.6206 EndY=-3.55 EndZ=0
    g21: LineSegment StartX=10.6206 StartY=-3.55 StartZ=0 EndX=4.12058 EndY=-3.55 EndZ=0
    g22: LineSegment StartX=4.12058 StartY=-3.55 StartZ=0 EndX=3.33722 EndY=-6.47354 EndZ=0
    g23: ArcOfCircle CenterX=6.23499 CenterY=-7.25 CenterZ=0 NormalX=0 NormalY=0 NormalZ=1 AngleXU=0 Radius=3 StartAngle=2.87979 EndAngle=6.02139
    g24: LineSegment StartX=71.2452 StartY=-6.05 StartZ=0 EndX=72.5302 EndY=-13.3376 EndZ=0
    g25: LineSegment StartX=83.023 StartY=2.05 StartZ=0 EndX=78.7784 EndY=-13.7912 EndZ=0
    g26: ArcOfCircle CenterX=75.717 CenterY=-12.7 CenterZ=0 NormalX=0 NormalY=0 NormalZ=1 AngleXU=0 Radius=3.25 StartAngle=3.33905 EndAngle=5.94078
    g27: LineSegment StartX=6.02302 StartY=3.55 StartZ=0 EndX=5.21917 EndY=0.55 EndZ=0
  constraints (72):
    c: Coincident(g0,g-10)
    c: Coincident(g0,g-9)
    c: Coincident(g1,g0)
    c: Coincident(g1,g-8)
    c: Coincident(g2,g1)
    c: Coincident(g2,g-8)
    c: Coincident(g3,g2)
    c: Coincident(g3,g-7)
    c: Horizontal(g4)
    c: Horizontal(g5)
    c: DistanceY(g5,g-11) = 1.5
    c: DistanceY(g0,g4) = 1.5
    c: Coincident(g6,g4)
    c: Coincident(g7,g6)
    c: Coincident(g8,g7)
    c: Coincident(g5,g8)
    c: Parallel(g-11,g8)
    c: PointOnObject(g9,g8)
    c: PointOnObject(g9,g-11)
    c: Distance(g5,g9) = 4
    c: Angle(g8,g9) = 1.5708
    c: DistanceX(g9,g9) = 1.5
    c: Coincident(g7,g-12)
    c: Parallel(g6,g-10)
    c: PointOnObject(g5,g-6)
    c: Coincident(g10,g5)
    c: Coincident(g10,g-6)
    c: Coincident(g11,g-11)
    c: Coincident(g11,g-3)
    c: Coincident(g12,g11)
    c: Coincident(g12,g-4)
    c: Coincident(g13,g12)
    c: Coincident(g13,g-4)
    c: Coincident(g14,g13)
    c: Coincident(g14,g-5)
    c: Coincident(g15,g14)
    c: Coincident(g15,g10)
    c: Coincident(g16,g10)
    c: Coincident(g16,g5)
    c: Radius(g-12) = 3.25
    c: PointOnObject(g17,g6)
    c: PointOnObject(g17,g-10)
    c: Angle(g17,g6) = 1.5708
    c: Distance(g17,g0) = 2.5
    c: Distance(g17) = 1.5
    c: Coincident(g18,g-12)
    c: Coincident(g18,g6)
    c: Coincident(g19,g6)
    c: Coincident(g19,g7)
    c: Angle(g19,g18) = 3.14159
    c: Coincident(g20,g4)
    c: Vertical(g20)
    c: Coincident(g21,g20)
    c: PointOnObject(g21,g-6)
    c: Horizontal(g21)
    c: Coincident(g22,g21)
    c: Coincident(g22,g-7)
    c: DistanceX(g21,g21) = 6.5
    c: DistanceY(g-13,g-13) = 1
    c: DistanceY(g20,g20) = 1
    c: Coincident(g23,g22)
    c: Coincident(g23,g3)
    c: Tangent(g23,g-7)
    c: Coincident(g24,g0)
    c: Coincident(g24,g18)
    c: Coincident(g25,g11)
    c: Coincident(g25,g-12)
    c: Coincident(g26,g25)
    c: Coincident(g26,g18)
    c: Tangent(g26,g-12)
    c: Coincident(g27,g10)
    c: Coincident(g27,g5)
FEATURE [PartDesign::Pad] Pad025
  BaseFeature = -> Chamfer
  Direction = (0,0,-1)
  Length = 1.425
  Length2 = 10
  Profile = -> Sketch039
  ReferenceAxis = -> Sketch039 [N_Axis]
  Refine = true
  Suppressed = false
  Type = 0
FEATURE [Sketcher::SketchObject] Sketch040
  ArcFitTolerance = 1e-06
  AttachmentSupport = -> [Pad025]
  ExternalGeometry = -> [Pad025]
  FullyConstrained = true
  MakeInternals = false
  MapMode = 5
  Placement = pos=(0,0,5.25) rot=(0,0,1;0rad)
  sketch-geometry (1):
    g0: Circle CenterX=75.717 CenterY=12.7 CenterZ=0 NormalX=0 NormalY=0 NormalZ=1 AngleXU=0 Radius=3.25
  constraints (2):
    c: Coincident(g0,g-3)
    c: Equal(g0,g-3)
FEATURE [PartDesign::Pad] Pad026
  BaseFeature = -> Pad025
  Direction = (0,0,1)
  Length = 0.25
  Length2 = 10
  Profile = -> Sketch040
  ReferenceAxis = -> Sketch040 [N_Axis]
  Refine = true
  Suppressed = false
  Type = 0
FEATURE [Sketcher::SketchObject] Sketch041
  ArcFitTolerance = 1e-06
  AttachmentSupport = -> [Pad026]
  ExternalGeometry = -> [Pad026]
  FullyConstrained = true
  MakeInternals = false
  MapMode = 5
  Placement = pos=(0,0,4.25) rot=(0,0,1;0rad)
  sketch-geometry (5):
    g0: LineSegment StartX=16.4156 StartY=4 StartZ=0 EndX=16.4156 EndY=9e-16 EndZ=0
    g1: LineSegment StartX=16.4156 StartY=9e-16 StartZ=0 EndX=30.2156 EndY=9e-16 EndZ=0
    g2: LineSegment StartX=30.2156 StartY=9e-16 StartZ=0 EndX=30.2156 EndY=4 EndZ=0
    g3: LineSegment StartX=30.2156 StartY=4 StartZ=0 EndX=16.4156 EndY=4 EndZ=0
    g4: LineSegment [constr] StartX=34.4156 StartY=6.05 StartZ=0 EndX=34.4156 EndY=-2.05 EndZ=0
  constraints (17):
    c: Coincident(g0,g1)
    c: Coincident(g1,g2)
    c: Coincident(g2,g3)
    c: Coincident(g3,g0)
    c: Vertical(g0)
    c: Vertical(g2)
    c: Horizontal(g1)
    c: Horizontal(g3)
    c: DistanceX(g3,g3) = 13.8
    c: DistanceY(g0,g0) = 4
    c: PointOnObject(g4,g-3)
    c: PointOnObject(g4,g-4)
    c: Vertical(g4)
    c: DistanceY(g4,g4) = 8.1
    c: DistanceX(g-4,g4) = 18
    c: DistanceY(g2,g4) = 2.05
    c: DistanceX(g-4,g0) = 0
FEATURE [PartDesign::Pocket] Pocket016
  BaseFeature = -> Pad026
  Direction = (0,0,-1)
  Length = 0.5
  Length2 = 5
  Profile = -> Sketch041
  ReferenceAxis = -> Sketch041 [N_Axis]
  Refine = true
  Suppressed = false
  Type = 0
FEATURE [Sketcher::SketchObject] Sketch042
  ArcFitTolerance = 1e-06
  AttachmentSupport = -> [Pocket016]
  ExternalGeometry = -> [Pocket016]
  FullyConstrained = true
  MakeInternals = false
  MapMode = 5
  Placement = pos=(0,0,4.25) rot=(0,0,1;0rad)
  sketch-geometry (6):
    g0: LineSegment StartX=35.2156 StartY=-2.05 StartZ=0 EndX=62.2156 EndY=-2.05 EndZ=0
    g1: LineSegment StartX=62.2156 StartY=-2.05 StartZ=0 EndX=62.2156 EndY=2.95 EndZ=0
    g2: LineSegment StartX=62.2156 StartY=2.95 StartZ=0 EndX=56.7156 EndY=6.05 EndZ=0
    g3: LineSegment StartX=56.7156 StartY=6.05 StartZ=0 EndX=46.7156 EndY=6.05 EndZ=0
    g4: LineSegment StartX=35.2156 StartY=-2.05 StartZ=0 EndX=35.2156 EndY=3.45 EndZ=0
    g5: LineSegment StartX=35.2156 StartY=3.45 StartZ=0 EndX=46.7156 EndY=6.05 EndZ=0
  constraints (18):
    c: PointOnObject(g0,g-4)
    c: PointOnObject(g0,g-4)
    c: Coincident(g1,g0)
    c: Vertical(g1)
    c: Coincident(g2,g1)
    c: PointOnObject(g2,g-3)
    c: Coincident(g3,g2)
    c: Coincident(g4,g0)
    c: Vertical(g4)
    c: Coincident(g5,g4)
    c: Coincident(g5,g3)
    c: DistanceX(g0,g0) = 27
    c: DistanceX(g3,g3) = 10
    c: DistanceY(g4,g4) = 5.5
    c: DistanceY(g1,g1) = 5
    c: DistanceX(g2,g1) = 5.5
    c: PointOnObject(g3,g-3)
    c: DistanceX(g-5,g0) = 5
FEATURE [PartDesign::Pad] Pad027
  BaseFeature = -> Pocket016
  Direction = (0,0,1)
  Length = 0.5
  Length2 = 10
  Profile = -> Sketch042
  ReferenceAxis = -> Sketch042 [N_Axis]
  Refine = true
  Suppressed = false
  Type = 0
FEATURE [Sketcher::SketchObject] Sketch043
  ArcFitTolerance = 1e-06
  AttachmentSupport = -> [Pad027]
  ExternalGeometry = -> [Pad027]
  FullyConstrained = true
  MakeInternals = false
  MapMode = 5
  Placement = pos=(0,0,4.75) rot=(0,0,1;0rad)
  sketch-geometry (3):
    g0: Circle CenterX=55.5156 CenterY=1.45 CenterZ=0 NormalX=0 NormalY=0 NormalZ=1 AngleXU=0 Radius=1.5
    g1: Circle CenterX=50.0156 CenterY=1.45 CenterZ=0 NormalX=0 NormalY=0 NormalZ=1 AngleXU=0 Radius=1.5
    g2: Circle CenterX=44.5156 CenterY=1.45 CenterZ=0 NormalX=0 NormalY=0 NormalZ=1 AngleXU=0 Radius=1.5
  constraints (9):
    c: Diameter(g2) = 3
    c: Diameter(g1) = 3
    c: Diameter(g0) = 3
    c: DistanceX(g1,g0) = 5.5
    c: DistanceX(g2,g1) = 5.5
    c: DistanceY(g0,g1) = 0
    c: DistanceY(g2,g1) = 0
    c: DistanceY(g0,g-3) = 1.5
    c: DistanceX(g0,g-3) = 6.7
FEATURE [PartDesign::Pocket] Pocket017
  BaseFeature = -> Pad027
  Direction = (0,0,-1)
  Length = 0.5
  Length2 = 5
  Profile = -> Sketch043
  ReferenceAxis = -> Sketch043 [N_Axis]
  Refine = true
  Suppressed = false
  Type = 0
FEATURE [Sketcher::SketchObject] Sketch044
  ArcFitTolerance = 1e-06
  AttachmentSupport = -> [Pocket017]
  ExternalGeometry = -> [Pocket017]
  FullyConstrained = true
  MakeInternals = false
  MapMode = 5
  Placement = pos=(0,0,5.25) rot=(0,0,1;0rad)
  sketch-geometry (1):
    g0: Circle CenterX=6.23499 CenterY=7.25 CenterZ=0 NormalX=0 NormalY=0 NormalZ=1 AngleXU=0 Radius=1
  constraints (2):
    c: Coincident(g0,g-3)
    c: Diameter(g0) = 2
FEATURE [PartDesign::Pad] Pad028
  BaseFeature = -> Pocket017
  Direction = (0,0,1)
  Length = 0.5
  Length2 = 10
  Profile = -> Sketch044
  ReferenceAxis = -> Sketch044 [N_Axis]
  Refine = true
  Suppressed = false
  Type = 0
FEATURE [Sketcher::SketchObject] Sketch045
  ArcFitTolerance = 1e-06
  AttachmentSupport = -> [Pad028]
  ExternalGeometry = -> [Pad028]
  FullyConstrained = true
  MakeInternals = false
  MapMode = 5
  Placement = pos=(0,0,5.5) rot=(0,0,1;0rad)
  sketch-geometry (1):
    g0: Circle CenterX=75.717 CenterY=12.7 CenterZ=0 NormalX=0 NormalY=0 NormalZ=1 AngleXU=0 Radius=1.5
  constraints (2):
    c: Coincident(g0,g-3)
    c: Diameter(g0) = 3
FEATURE [PartDesign::Pad] Pad029
  BaseFeature = -> Pad028
  Direction = (0,0,1)
  Length = 1.1
  Length2 = 10
  Profile = -> Sketch045
  ReferenceAxis = -> Sketch045 [N_Axis]
  Refine = true
  Suppressed = false
  Type = 0
FEATURE [Sketcher::SketchObject] Sketch046
  ArcFitTolerance = 1e-06
  AttachmentSupport = -> [Pad029]
  ExternalGeometry = -> [Pad029]
  FullyConstrained = true
  MakeInternals = false
  MapMode = 5
  Placement = pos=(0,0,2.75) rot=(1,0,0;3.14159rad)
  sketch-geometry (2):
    g0: Circle CenterX=64.3134 CenterY=-2 CenterZ=0 NormalX=0 NormalY=0 NormalZ=1 AngleXU=0 Radius=1
    g1: Circle CenterX=75.717 CenterY=-2 CenterZ=0 NormalX=0 NormalY=0 NormalZ=1 AngleXU=0 Radius=1
  constraints (7):
    c: Diameter(g0) = 2
    c: Diameter(g1) = 2
    c: DistanceY(g-4,g-3) = 5.1
    c: DistanceY(g0,g-3) = 2.55
    c: DistanceY(g0,g1) = 0
    c: DistanceX(g1,g-5) = 0
    c: DistanceX(g0,g-3) = 16.7
FEATURE [PartDesign::Pad] Pad030
  BaseFeature = -> Pad029
  Direction = (0,0,-1)
  Length = 2.7
  Length2 = 10
  Profile = -> Sketch046
  ReferenceAxis = -> Sketch046 [N_Axis]
  Refine = true
  Suppressed = false
  Type = 0
FEATURE [Sketcher::SketchObject] Sketch047
  ArcFitTolerance = 1e-06
  AttachmentSupport = -> [Pad030]
  ExternalGeometry = -> [Pad030]
  FullyConstrained = true
  MakeInternals = false
  MapMode = 5
  Placement = pos=(0,0,2.75) rot=(1,0,0;3.14159rad)
  sketch-geometry (1):
    g0: Circle CenterX=75.717 CenterY=-12.7 CenterZ=0 NormalX=0 NormalY=0 NormalZ=1 AngleXU=0 Radius=1.5
  constraints (2):
    c: Coincident(g0,g-3)
    c: Diameter(g0) = 3
FEATURE [PartDesign::Pad] Pad031
  BaseFeature = -> Pad030
  Direction = (0,0,-1)
  Length = 6.5
  Length2 = 10
  Profile = -> Sketch047
  ReferenceAxis = -> Sketch047 [N_Axis]
  Refine = true
  Suppressed = false
  Type = 0
FEATURE [Sketcher::SketchObject] Sketch048
  ArcFitTolerance = 1e-06
  AttachmentSupport = -> [Pad031]
  ExternalGeometry = -> [Pad031]
  FullyConstrained = true
  MakeInternals = false
  MapMode = 5
  Placement = pos=(0,0,2.75) rot=(1,0,0;3.14159rad)
  sketch-geometry (4):
    g0: LineSegment StartX=74.0014 StartY=-13.0432 StartZ=0 EndX=75.717 EndY=-12.7 EndZ=0
    g1: LineSegment StartX=75.717 StartY=-12.7 StartZ=0 EndX=77.4631 EndY=-12.7 EndZ=0
    g2: LineSegment StartX=77.4631 StartY=-12.7 StartZ=0 EndX=77.2256 EndY=-13.5862 EndZ=0
    g3: ArcOfCircle CenterX=75.717 CenterY=-12.7 CenterZ=0 NormalX=0 NormalY=0 NormalZ=1 AngleXU=0 Radius=1.7496 StartAngle=3.33905 EndAngle=5.75207
  constraints (10):
    c: Coincident(g0,g-4)
    c: Coincident(g0,g-4)
    c: Coincident(g1,g0)
    c: PointOnObject(g1,g-5)
    c: Horizontal(g1)
    c: Coincident(g2,g1)
    c: Coincident(g2,g-5)
    c: Coincident(g3,g0)
    c: Coincident(g3,g2)
    c: Tangent(g3,g-4)
FEATURE [PartDesign::Pad] Pad032
  BaseFeature = -> Pad031
  Direction = (0,0,-1)
  Length = 1.425
  Length2 = 10
  Profile = -> Sketch048
  ReferenceAxis = -> Sketch048 [N_Axis]
  Refine = true
  Suppressed = false
  Type = 0
FEATURE [Sketcher::SketchObject] Sketch049
  ArcFitTolerance = 1e-06
  AttachmentSupport = -> [Pad032]
  ExternalGeometry = -> [Pad032]
  FullyConstrained = true
  MakeInternals = false
  MapMode = 5
  Placement = pos=(0,0,1.325) rot=(1,0,0;3.14159rad)
  sketch-geometry (1):
    g0: Circle CenterX=6.23499 CenterY=-7.25 CenterZ=0 NormalX=0 NormalY=0 NormalZ=1 AngleXU=0 Radius=1.15
  constraints (2):
    c: Coincident(g0,g-3)
    c: Diameter(g0) = 2.3
FEATURE [PartDesign::Pad] Pad033
  BaseFeature = -> Pad032
  Direction = (0,0,-1)
  Length = 4.5
  Length2 = 10
  Profile = -> Sketch049
  ReferenceAxis = -> Sketch049 [N_Axis]
  Refine = true
  Suppressed = false
  Type = 0
FEATURE [PartDesign::Pocket] Pocket024
  BaseFeature = -> Pad033
  Direction = (0,0,1)
  Length = 0.05
  Length2 = 5
  Profile = -> Pad033 [Face2]
  Refine = true
  Suppressed = false
  Type = 0
FEATURE [PartDesign::Pocket] Pocket025
  BaseFeature = -> Pocket024
  Direction = (0,1,0)
  Length = 0.1
  Length2 = 5
  Profile = -> Pocket024 [Face58]
  Refine = true
  Suppressed = false
  Type = 0
FEATURE [PartDesign::Chamfer] Chamfer004
  Angle = 45
  Base = -> Pocket025 [Edge136]
  BaseFeature = -> Pocket025
  ChamferType = 0
  FlipDirection = false
  Refine = true
  Size = 0.249
  Size2 = 1
  SupportTransform = false
  Suppressed = false
  UseAllEdges = false
FEATURE [PartDesign::Body] Body002  label="Outer_Left_Crane_Boom"
  AllowCompound = false
  Group = -> [Binder,Sketch036,Pad021,Sketch037,Pad022,Pad023,Sketch038,Pad024,Chamfer,Sketch039,Pad025,Sketch040,Pad026,Sketch041,Pocket016,Sketch042,Pad027,Sketch043,Pocket017,Sketch044,Pad028,Sketch045,Pad029,Sketch046,Pad030,Sketch047,Pad031,Sketch048,Pad032,Sketch049,Pad033,Pocket024,Pocket025,Chamfer004]
  Origin = -> Origin002
  Placement = pos=(19.43,-36.85,26.35) rot=(0.57735,0.57735,-0.57735;4.18879rad)
  Tip = -> Chamfer004
COMPONENT P3 — recipe-attached ("Pre_Outer_Right_Crane_Boom", modeled in this document).
Construction recipe (the document's own serialized feature program — sketch geometry with constraints, then the solid features built on it; lengths are millimeters unless a unit is written):

FEATURE [PartDesign::SubShapeBinder] Binder001
  BindCopyOnChange = 0
  BindMode = 2
  ClaimChildren = false
  Context = -> Body003 [Binder001.]
  Fuse = false
  MakeFace = true
  OffsetFill = false
  OffsetIntersection = false
  OffsetJoinType = 0
  OffsetOpenResult = false
  PartialLoad = false
  Refine = true
  Relative = true
  _Version = 2
FEATURE [Sketcher::SketchObject] Sketch050
  ArcFitTolerance = 1e-06
  AttachmentSupport = -> [Binder001]
  ExternalGeometry = -> [Binder001]
  FullyConstrained = true
  MakeInternals = false
  MapMode = 5
  Placement = pos=(0,0,2.75) rot=(0,0,1;0rad)
  sketch-geometry (18):
    g0: LineSegment StartX=16.4156 StartY=-2.05 StartZ=0 EndX=83.023 EndY=-2.05 EndZ=0
    g1: LineSegment StartX=83.023 StartY=-2.05 StartZ=0 EndX=78.7784 EndY=13.7912 EndZ=0
    g2: ArcOfCircle CenterX=75.717 CenterY=12.7 CenterZ=0 NormalX=0 NormalY=0 NormalZ=1 AngleXU=0 Radius=3.25 StartAngle=0.3424 EndAngle=2.94413
    g3: LineSegment StartX=72.5302 StartY=13.3376 StartZ=0 EndX=71.2452 EndY=6.05 EndZ=0
    g4: LineSegment StartX=71.2452 StartY=6.05 StartZ=0 EndX=14.2452 EndY=6.05 EndZ=0
    g5: LineSegment StartX=14.2452 StartY=6.05 StartZ=0 EndX=14.004 EndY=6.95 EndZ=0
    g6: LineSegment StartX=14.004 StartY=6.95 StartZ=0 EndX=9.42121 EndY=6.95 EndZ=0
    g7: LineSegment StartX=9.42121 StartY=6.95 StartZ=0 EndX=9.13277 EndY=8.02646 EndZ=0
    g8: ArcOfCircle CenterX=6.23499 CenterY=7.25 CenterZ=0 NormalX=0 NormalY=0 NormalZ=1 AngleXU=0 Radius=3 StartAngle=0.261799 EndAngle=3.40339
    g9: LineSegment StartX=3.33722 StartY=6.47354 StartZ=0 EndX=6.02302 EndY=-3.55 EndZ=0
    g10: LineSegment StartX=16.6835 StartY=-3.05 StartZ=0 EndX=16.4156 EndY=-2.05 EndZ=0
    g11: LineSegment StartX=6.02302 StartY=-3.55 StartZ=0 EndX=12.2347 EndY=-3.55 EndZ=0
    g12: LineSegment StartX=12.2347 StartY=-3.55 StartZ=0 EndX=12.1007 EndY=-3.05 EndZ=0
    g13: LineSegment StartX=12.1007 StartY=-3.05 StartZ=0 EndX=16.6835 EndY=-3.05 EndZ=0
    g14: LineSegment [constr] StartX=14.2452 StartY=6.05 StartZ=0 EndX=16.4156 EndY=-2.05 EndZ=0
    g15: LineSegment [constr] StartX=9.42121 StartY=6.95 StartZ=0 EndX=12.1007 EndY=-3.05 EndZ=0
    g16: LineSegment [constr] StartX=6.23499 StartY=7.25 StartZ=0 EndX=3.33722 EndY=6.47354 EndZ=0
    g17: LineSegment [constr] StartX=6.23499 StartY=7.25 StartZ=0 EndX=9.13277 EndY=8.02646 EndZ=0
  constraints (53):
    c: Horizontal(g0)
    c: Coincident(g1,g0)
    c: Coincident(g2,g1)
    c: Coincident(g3,g2)
    c: Coincident(g4,g3)
    c: Horizontal(g4)
    c: Coincident(g5,g4)
    c: Coincident(g6,g5)
    c: Horizontal(g6)
    c: Coincident(g7,g6)
    c: Coincident(g8,g7)
    c: Coincident(g9,g8)
    c: Coincident(g10,g0)
    c: Coincident(g11,g9)
    c: Horizontal(g11)
    c: Coincident(g12,g11)
    c: Coincident(g13,g12)
    c: Coincident(g13,g10)
    c: Horizontal(g13)
    c: DistanceX(g9,g0) = 77
    c: DistanceY(g0,g4) = 8.1
    c: Diameter(g2) = 6.5
    c: Diameter(g8) = 6
    c: DistanceX(g4,g4) = 57
    c: DistanceY(g0,g2) = 14.75
    c: Angle(g1,g0) = 1.309
    c: Angle(g3,g1) = 0.436332
    c: Distance(g1) = 16.4
    c: Distance(g3) = 7.4
    c: Coincident(g14,g4)
    c: Coincident(g14,g0)
    c: Coincident(g15,g6)
    c: Coincident(g15,g12)
    c: Parallel(g7,g15)
    c: Parallel(g5,g14)
    c: Parallel(g10,g14)
    c: Parallel(g12,g15)
    c: Parallel(g15,g14)
    c: Parallel(g15,g9)
    c: Parallel(g1,g14)
    c: DistanceY(g-3,g-3) = 4
    c: DistanceY(g-3,g4) = 2.05
    c: DistanceY(g12,g5) = 10
    c: DistanceY(g10,g0) = 1
    c: DistanceY(g11,g12) = 0.5
    c: Coincident(g16,g8)
    c: Coincident(g16,g8)
    c: Coincident(g17,g8)
    c: Coincident(g17,g7)
    c: Angle(g16,g17) = 3.14159
    c: Angle(g17,g7) = 1.5708
    c: PointOnObject(g-3,g9)
    c: DistanceY(g9,g8) = 10.8
FEATURE [PartDesign::Pad] Pad034
  Direction = (0,0,1)
  Length = 1.5
  Length2 = 10
  Profile = -> Sketch050
  ReferenceAxis = -> Sketch050 [N_Axis]
  Refine = true
  Suppressed = false
  Type = 0
FEATURE [Sketcher::SketchObject] Sketch051
  ArcFitTolerance = 1e-06
  AttachmentSupport = -> [Pad034]
  ExternalGeometry = -> [Pad034]
  FullyConstrained = true
  MakeInternals = false
  MapMode = 5
  Placement = pos=(0,0,4.25) rot=(0,0,1;0rad)
  sketch-geometry (12):
    g0: LineSegment StartX=14.004 StartY=6.95 StartZ=0 EndX=16.6835 EndY=-3.05 EndZ=0
    g1: LineSegment StartX=16.6835 StartY=-3.05 StartZ=0 EndX=12.1007 EndY=-3.05 EndZ=0
    g2: LineSegment StartX=12.1007 StartY=-3.05 StartZ=0 EndX=12.2347 EndY=-3.55 EndZ=0
    g3: LineSegment StartX=12.2347 StartY=-3.55 StartZ=0 EndX=6.02302 EndY=-3.55 EndZ=0
    g4: LineSegment StartX=6.02302 StartY=-3.55 StartZ=0 EndX=3.33722 EndY=6.47354 EndZ=0
    g5: LineSegment StartX=14.004 StartY=6.95 StartZ=0 EndX=9.42121 EndY=6.95 EndZ=0
    g6: LineSegment StartX=9.42121 StartY=6.95 StartZ=0 EndX=9.13277 EndY=8.02646 EndZ=0
    g7: ArcOfCircle CenterX=6.23499 CenterY=7.25 CenterZ=0 NormalX=0 NormalY=0 NormalZ=1 AngleXU=0 Radius=3 StartAngle=0.261799 EndAngle=3.40339
    g8: LineSegment StartX=72.5302 StartY=13.3376 StartZ=0 EndX=69.8169 EndY=-2.05 EndZ=0
    g9: LineSegment StartX=78.7784 StartY=13.7912 StartZ=0 EndX=83.023 EndY=-2.05 EndZ=0
    g10: LineSegment StartX=83.023 StartY=-2.05 StartZ=0 EndX=69.8169 EndY=-2.05 EndZ=0
    g11: ArcOfCircle CenterX=75.717 CenterY=12.7 CenterZ=0 NormalX=0 NormalY=0 NormalZ=1 AngleXU=0 Radius=3.25 StartAngle=0.342399 EndAngle=2.94414
  constraints (27):
    c: Coincident(g0,g-7)
    c: Coincident(g0,g-10)
    c: Coincident(g1,g0)
    c: Coincident(g1,g-11)
    c: Coincident(g2,g1)
    c: Coincident(g2,g-11)
    c: Coincident(g3,g2)
    c: Coincident(g3,g-5)
    c: Coincident(g4,g3)
    c: Coincident(g4,g-4)
    c: Coincident(g5,g0)
    c: Coincident(g5,g-8)
    c: Coincident(g6,g5)
    c: Coincident(g6,g-8)
    c: Coincident(g7,g4)
    c: Coincident(g7,g6)
    c: Tangent(g7,g-3)
    c: Coincident(g8,g-14)
    c: PointOnObject(g8,g-15)
    c: Coincident(g9,g-14)
    c: Coincident(g9,g-15)
    c: Coincident(g10,g9)
    c: Coincident(g10,g8)
    c: PointOnObject(g-13,g8)
    c: Coincident(g11,g8)
    c: Coincident(g11,g9)
    c: Tangent(g11,g-14)
FEATURE [PartDesign::Pad] Pad035
  BaseFeature = -> Pad034
  Direction = (0,0,1)
  Length = 1
  Length2 = 10
  Profile = -> Sketch051
  ReferenceAxis = -> Sketch051 [N_Axis]
  Refine = true
  Suppressed = false
  Type = 0
FEATURE [PartDesign::Pad] Pad036
  BaseFeature = -> Pad035
  Direction = (0,0,1)
  Length = 1
  Length2 = 10
  Profile = -> Sketch051
  ReferenceAxis = -> Sketch051 [N_Axis]
  Refine = true
  Suppressed = false
  Type = 0
FEATURE [Sketcher::SketchObject] Sketch052
  ArcFitTolerance = 1e-06
  AttachmentSupport = -> [Pad036]
  ExternalGeometry = -> [Pad036]
  FullyConstrained = true
  MakeInternals = false
  MapMode = 5
  Placement = pos=(0,0,4.25) rot=(0,0,1;0rad)
  sketch-geometry (4):
    g0: LineSegment StartX=70.2452 StartY=6.05 StartZ=0 EndX=68.8169 EndY=-2.05 EndZ=0
    g1: LineSegment StartX=69.8169 StartY=-2.05 StartZ=0 EndX=68.8169 EndY=-2.05 EndZ=0
    g2: LineSegment StartX=69.8169 StartY=-2.05 StartZ=0 EndX=71.2452 EndY=6.05 EndZ=0
    g3: LineSegment StartX=70.2452 StartY=6.05 StartZ=0 EndX=71.2452 EndY=6.05 EndZ=0
  constraints (10):
    c: PointOnObject(g0,g-4)
    c: PointOnObject(g0,g-5)
    c: Coincident(g1,g-5)
    c: Coincident(g1,g0)
    c: Coincident(g2,g1)
    c: Coincident(g2,g-4)
    c: Coincident(g3,g0)
    c: Coincident(g3,g2)
    c: DistanceX(g3,g3) = 1
    c: DistanceX(g1,g1) = 1
FEATURE [PartDesign::Pad] Pad037
  BaseFeature = -> Pad036
  Direction = (0,0,1)
  Length = 1
  Length2 = 10
  Profile = -> Sketch052
  ReferenceAxis = -> Sketch052 [N_Axis]
  Refine = true
  Suppressed = false
  Type = 0
FEATURE [PartDesign::Chamfer] Chamfer001
  Angle = 45
  Base = -> Pad037 [Edge52]
  BaseFeature = -> Pad037
  ChamferType = 0
  FlipDirection = false
  Refine = true
  Size = 0.99
  Size2 = 1
  SupportTransform = false
  Suppressed = false
  UseAllEdges = false
FEATURE [Sketcher::SketchObject] Sketch053
  ArcFitTolerance = 1e-06
  AttachmentSupport = -> [Chamfer001]
  ExternalGeometry = -> [Chamfer001,Binder001]
  FullyConstrained = true
  MakeInternals = false
  MapMode = 5
  Placement = pos=(0,0,2.75) rot=(1,0,0;3.14159rad)
  sketch-geometry (28):
    g0: LineSegment StartX=71.2452 StartY=-6.05 StartZ=0 EndX=14.2452 EndY=-6.05 EndZ=0
    g1: LineSegment StartX=14.2452 StartY=-6.05 StartZ=0 EndX=14.004 EndY=-6.95 EndZ=0
    g2: LineSegment StartX=14.004 StartY=-6.95 StartZ=0 EndX=9.42121 EndY=-6.95 EndZ=0
    g3: LineSegment StartX=9.42121 StartY=-6.95 StartZ=0 EndX=9.13277 EndY=-8.02646 EndZ=0
    g4: LineSegment StartX=72.5038 StartY=-4.55 StartZ=0 EndX=10.6206 EndY=-4.55 EndZ=0
    g5: LineSegment StartX=81.0134 StartY=0.55 StartZ=0 EndX=5.21917 EndY=0.55 EndZ=0
    g6: LineSegment StartX=72.5038 StartY=-4.55 StartZ=0 EndX=74.0014 EndY=-13.0432 EndZ=0
    g7: ArcOfCircle CenterX=75.717 CenterY=-12.7 CenterZ=0 NormalX=0 NormalY=0 NormalZ=1 AngleXU=0 Radius=1.74961 StartAngle=3.33905 EndAngle=5.75206
    g8: LineSegment StartX=77.2256 StartY=-13.5862 StartZ=0 EndX=81.0134 EndY=0.55 EndZ=0
    g9: LineSegment [constr] StartX=79.9781 StartY=-3.3137 StartZ=0 EndX=81.4781 EndY=-3.71563 EndZ=0
    g10: LineSegment StartX=5.21917 StartY=0.55 StartZ=0 EndX=6.02302 EndY=3.55 EndZ=0
    g11: LineSegment StartX=83.023 StartY=2.05 StartZ=0 EndX=16.4156 EndY=2.05 EndZ=0
    g12: LineSegment StartX=16.4156 StartY=2.05 StartZ=0 EndX=16.6835 EndY=3.05 EndZ=0
    g13: LineSegment StartX=16.6835 StartY=3.05 StartZ=0 EndX=12.1007 EndY=3.05 EndZ=0
    g14: LineSegment StartX=12.1007 StartY=3.05 StartZ=0 EndX=12.2347 EndY=3.55 EndZ=0
    g15: LineSegment StartX=12.2347 StartY=3.55 StartZ=0 EndX=6.02302 EndY=3.55 EndZ=0
    g16: LineSegment StartX=6.02302 StartY=3.55 StartZ=0 EndX=5.21917 EndY=0.55 EndZ=0
    g17: LineSegment [constr] StartX=73.1565 StartY=-8.25155 StartZ=0 EndX=71.6793 EndY=-8.51202 EndZ=0
    g18: LineSegment [constr] StartX=72.5302 StartY=-13.3376 StartZ=0 EndX=74.0014 EndY=-13.0432 EndZ=0
    g19: LineSegment [constr] StartX=74.0014 StartY=-13.0432 StartZ=0 EndX=75.717 EndY=-12.7 EndZ=0
    g20: LineSegment StartX=10.6206 StartY=-4.55 StartZ=0 EndX=10.6206 EndY=-3.55 EndZ=0
    g21: LineSegment StartX=10.6206 StartY=-3.55 StartZ=0 EndX=4.12058 EndY=-3.55 EndZ=0
    g22: LineSegment StartX=4.12058 StartY=-3.55 StartZ=0 EndX=3.33722 EndY=-6.47354 EndZ=0
    g23: ArcOfCircle CenterX=6.23499 CenterY=-7.25 CenterZ=0 NormalX=0 NormalY=0 NormalZ=1 AngleXU=0 Radius=3 StartAngle=2.87979 EndAngle=6.02139
    g24: LineSegment StartX=71.2452 StartY=-6.05 StartZ=0 EndX=72.5302 EndY=-13.3376 EndZ=0
    g25: LineSegment StartX=83.023 StartY=2.05 StartZ=0 EndX=78.7784 EndY=-13.7912 EndZ=0
    g26: ArcOfCircle CenterX=75.717 CenterY=-12.7 CenterZ=0 NormalX=0 NormalY=0 NormalZ=1 AngleXU=0 Radius=3.25 StartAngle=3.33905 EndAngle=5.94078
    g27: LineSegment StartX=6.02302 StartY=3.55 StartZ=0 EndX=5.21917 EndY=0.55 EndZ=0
  constraints (72):
    c: Coincident(g0,g-10)
    c: Coincident(g0,g-9)
    c: Coincident(g1,g0)
    c: Coincident(g1,g-8)
    c: Coincident(g2,g1)
    c: Coincident(g2,g-8)
    c: Coincident(g3,g2)
    c: Coincident(g3,g-7)
    c: Horizontal(g4)
    c: Horizontal(g5)
    c: DistanceY(g5,g-11) = 1.5
    c: DistanceY(g0,g4) = 1.5
    c: Coincident(g6,g4)
    c: Coincident(g7,g6)
    c: Coincident(g8,g7)
    c: Coincident(g5,g8)
    c: Parallel(g-11,g8)
    c: PointOnObject(g9,g8)
    c: PointOnObject(g9,g-11)
    c: Distance(g5,g9) = 4
    c: Angle(g8,g9) = 1.5708
    c: DistanceX(g9,g9) = 1.5
    c: Coincident(g7,g-12)
    c: Parallel(g6,g-10)
    c: PointOnObject(g5,g-6)
    c: Coincident(g10,g5)
    c: Coincident(g10,g-6)
    c: Coincident(g11,g-11)
    c: Coincident(g11,g-3)
    c: Coincident(g12,g11)
    c: Coincident(g12,g-4)
    c: Coincident(g13,g12)
    c: Coincident(g13,g-4)
    c: Coincident(g14,g13)
    c: Coincident(g14,g-5)
    c: Coincident(g15,g14)
    c: Coincident(g15,g10)
    c: Coincident(g16,g10)
    c: Coincident(g16,g5)
    c: Radius(g-12) = 3.25
    c: PointOnObject(g17,g6)
    c: PointOnObject(g17,g-10)
    c: Angle(g17,g6) = 1.5708
    c: Distance(g17,g0) = 2.5
    c: Distance(g17) = 1.5
    c: Coincident(g18,g-12)
    c: Coincident(g18,g6)
    c: Coincident(g19,g6)
    c: Coincident(g19,g7)
    c: Angle(g19,g18) = 3.14159
    c: Coincident(g20,g4)
    c: Vertical(g20)
    c: Coincident(g21,g20)
    c: PointOnObject(g21,g-6)
    c: Horizontal(g21)
    c: Coincident(g22,g21)
    c: Coincident(g22,g-7)
    c: DistanceX(g21,g21) = 6.5
    c: DistanceY(g-13,g-13) = 1
    c: DistanceY(g20,g20) = 1
    c: Coincident(g23,g22)
    c: Coincident(g23,g3)
    c: Tangent(g23,g-7)
    c: Coincident(g24,g0)
    c: Coincident(g24,g18)
    c: Coincident(g25,g11)
    c: Coincident(g25,g-12)
    c: Coincident(g26,g25)
    c: Coincident(g26,g18)
    c: Tangent(g26,g-12)
    c: Coincident(g27,g10)
    c: Coincident(g27,g5)
FEATURE [PartDesign::Pad] Pad038
  BaseFeature = -> Chamfer001
  Direction = (0,0,-1)
  Length = 1.425
  Length2 = 10
  Profile = -> Sketch053
  ReferenceAxis = -> Sketch053 [N_Axis]
  Refine = true
  Suppressed = false
  Type = 0
FEATURE [Sketcher::SketchObject] Sketch054
  ArcFitTolerance = 1e-06
  AttachmentSupport = -> [Pad038]
  ExternalGeometry = -> [Pad038]
  FullyConstrained = true
  MakeInternals = false
  MapMode = 5
  Placement = pos=(0,0,5.25) rot=(0,0,1;0rad)
  sketch-geometry (1):
    g0: Circle CenterX=75.717 CenterY=12.7 CenterZ=0 NormalX=0 NormalY=0 NormalZ=1 AngleXU=0 Radius=3.25
  constraints (2):
    c: Coincident(g0,g-3)
    c: Equal(g0,g-3)
FEATURE [PartDesign::Pad] Pad039
  BaseFeature = -> Pad038
  Direction = (0,0,1)
  Length = 0.25
  Length2 = 10
  Profile = -> Sketch054
  ReferenceAxis = -> Sketch054 [N_Axis]
  Refine = true
  Suppressed = false
  Type = 0
FEATURE [Sketcher::SketchObject] Sketch055
  ArcFitTolerance = 1e-06
  AttachmentSupport = -> [Pad039]
  ExternalGeometry = -> [Pad039]
  FullyConstrained = true
  MakeInternals = false
  MapMode = 5
  Placement = pos=(0,0,4.25) rot=(0,0,1;0rad)
  sketch-geometry (5):
    g0: LineSegment StartX=16.4156 StartY=4 StartZ=0 EndX=16.4156 EndY=9e-16 EndZ=0
    g1: LineSegment StartX=16.4156 StartY=9e-16 StartZ=0 EndX=30.2156 EndY=9e-16 EndZ=0
    g2: LineSegment StartX=30.2156 StartY=9e-16 StartZ=0 EndX=30.2156 EndY=4 EndZ=0
    g3: LineSegment StartX=30.2156 StartY=4 StartZ=0 EndX=16.4156 EndY=4 EndZ=0
    g4: LineSegment [constr] StartX=34.4156 StartY=6.05 StartZ=0 EndX=34.4156 EndY=-2.05 EndZ=0
  constraints (17):
    c: Coincident(g0,g1)
    c: Coincident(g1,g2)
    c: Coincident(g2,g3)
    c: Coincident(g3,g0)
    c: Vertical(g0)
    c: Vertical(g2)
    c: Horizontal(g1)
    c: Horizontal(g3)
    c: DistanceX(g3,g3) = 13.8
    c: DistanceY(g0,g0) = 4
    c: PointOnObject(g4,g-3)
    c: PointOnObject(g4,g-4)
    c: Vertical(g4)
    c: DistanceY(g4,g4) = 8.1
    c: DistanceX(g-4,g4) = 18
    c: DistanceY(g2,g4) = 2.05
    c: DistanceX(g-4,g0) = 0
FEATURE [PartDesign::Pocket] Pocket018
  BaseFeature = -> Pad039
  Direction = (0,0,-1)
  Length = 0.5
  Length2 = 5
  Profile = -> Sketch055
  ReferenceAxis = -> Sketch055 [N_Axis]
  Refine = true
  Suppressed = false
  Type = 0
FEATURE [Sketcher::SketchObject] Sketch056
  ArcFitTolerance = 1e-06
  AttachmentSupport = -> [Pocket018]
  ExternalGeometry = -> [Pocket018]
  FullyConstrained = true
  MakeInternals = false
  MapMode = 5
  Placement = pos=(0,0,4.25) rot=(0,0,1;0rad)
  sketch-geometry (6):
    g0: LineSegment StartX=35.2156 StartY=-2.05 StartZ=0 EndX=62.2156 EndY=-2.05 EndZ=0
    g1: LineSegment StartX=62.2156 StartY=-2.05 StartZ=0 EndX=62.2156 EndY=2.95 EndZ=0
    g2: LineSegment StartX=62.2156 StartY=2.95 StartZ=0 EndX=56.7156 EndY=6.05 EndZ=0
    g3: LineSegment StartX=56.7156 StartY=6.05 StartZ=0 EndX=46.7156 EndY=6.05 EndZ=0
    g4: LineSegment StartX=35.2156 StartY=-2.05 StartZ=0 EndX=35.2156 EndY=3.45 EndZ=0
    g5: LineSegment StartX=35.2156 StartY=3.45 StartZ=0 EndX=46.7156 EndY=6.05 EndZ=0
  constraints (18):
    c: PointOnObject(g0,g-4)
    c: PointOnObject(g0,g-4)
    c: Coincident(g1,g0)
    c: Vertical(g1)
    c: Coincident(g2,g1)
    c: PointOnObject(g2,g-3)
    c: Coincident(g3,g2)
    c: Coincident(g4,g0)
    c: Vertical(g4)
    c: Coincident(g5,g4)
    c: Coincident(g5,g3)
    c: DistanceX(g0,g0) = 27
    c: DistanceX(g3,g3) = 10
    c: DistanceY(g4,g4) = 5.5
    c: DistanceY(g1,g1) = 5
    c: DistanceX(g2,g1) = 5.5
    c: PointOnObject(g3,g-3)
    c: DistanceX(g-5,g0) = 5
FEATURE [PartDesign::Pad] Pad040
  BaseFeature = -> Pocket018
  Direction = (0,0,1)
  Length = 0.5
  Length2 = 10
  Profile = -> Sketch056
  ReferenceAxis = -> Sketch056 [N_Axis]
  Refine = true
  Suppressed = false
  Type = 0
FEATURE [Sketcher::SketchObject] Sketch057
  ArcFitTolerance = 1e-06
  AttachmentSupport = -> [Pad040]
  ExternalGeometry = -> [Pad040]
  FullyConstrained = true
  MakeInternals = false
  MapMode = 5
  Placement = pos=(0,0,4.75) rot=(0,0,1;0rad)
  sketch-geometry (3):
    g0: Circle CenterX=55.5156 CenterY=1.45 CenterZ=0 NormalX=0 NormalY=0 NormalZ=1 AngleXU=0 Radius=1.5
    g1: Circle CenterX=50.0156 CenterY=1.45 CenterZ=0 NormalX=0 NormalY=0 NormalZ=1 AngleXU=0 Radius=1.5
    g2: Circle CenterX=44.5156 CenterY=1.45 CenterZ=0 NormalX=0 NormalY=0 NormalZ=1 AngleXU=0 Radius=1.5
  constraints (9):
    c: Diameter(g2) = 3
    c: Diameter(g1) = 3
    c: Diameter(g0) = 3
    c: DistanceX(g1,g0) = 5.5
    c: DistanceX(g2,g1) = 5.5
    c: DistanceY(g0,g1) = 0
    c: DistanceY(g2,g1) = 0
    c: DistanceY(g0,g-3) = 1.5
    c: DistanceX(g0,g-3) = 6.7
FEATURE [PartDesign::Pocket] Pocket019
  BaseFeature = -> Pad040
  Direction = (0,0,-1)
  Length = 0.5
  Length2 = 5
  Profile = -> Sketch057
  ReferenceAxis = -> Sketch057 [N_Axis]
  Refine = true
  Suppressed = false
  Type = 0
FEATURE [Sketcher::SketchObject] Sketch058
  ArcFitTolerance = 1e-06
  AttachmentSupport = -> [Pocket019]
  ExternalGeometry = -> [Pocket019]
  FullyConstrained = true
  MakeInternals = false
  MapMode = 5
  Placement = pos=(0,0,5.25) rot=(0,0,1;0rad)
  sketch-geometry (1):
    g0: Circle CenterX=6.23499 CenterY=7.25 CenterZ=0 NormalX=0 NormalY=0 NormalZ=1 AngleXU=0 Radius=1
  constraints (2):
    c: Coincident(g0,g-3)
    c: Diameter(g0) = 2
FEATURE [PartDesign::Pad] Pad041
  BaseFeature = -> Pocket019
  Direction = (0,0,1)
  Length = 0.5
  Length2 = 10
  Profile = -> Sketch058
  ReferenceAxis = -> Sketch058 [N_Axis]
  Refine = true
  Suppressed = false
  Type = 0
FEATURE [Sketcher::SketchObject] Sketch059
  ArcFitTolerance = 1e-06
  AttachmentSupport = -> [Pad041]
  ExternalGeometry = -> [Pad041]
  FullyConstrained = true
  MakeInternals = false
  MapMode = 5
  Placement = pos=(0,0,5.5) rot=(0,0,1;0rad)
  sketch-geometry (1):
    g0: Circle CenterX=75.717 CenterY=12.7 CenterZ=0 NormalX=0 NormalY=0 NormalZ=1 AngleXU=0 Radius=1.5
  constraints (2):
    c: Coincident(g0,g-3)
    c: Diameter(g0) = 3
FEATURE [PartDesign::Pad] Pad042
  BaseFeature = -> Pad041
  Direction = (0,0,1)
  Length = 1.1
  Length2 = 10
  Profile = -> Sketch059
  ReferenceAxis = -> Sketch059 [N_Axis]
  Refine = true
  Suppressed = false
  Type = 0
FEATURE [Sketcher::SketchObject] Sketch060
  ArcFitTolerance = 1e-06
  AttachmentSupport = -> [Pad042]
  ExternalGeometry = -> [Pad042]
  FullyConstrained = true
  MakeInternals = false
  MapMode = 5
  Placement = pos=(0,0,2.75) rot=(1,0,0;3.14159rad)
  sketch-geometry (2):
    g0: Circle CenterX=64.3134 CenterY=-2 CenterZ=0 NormalX=0 NormalY=0 NormalZ=1 AngleXU=0 Radius=1
    g1: Circle CenterX=75.717 CenterY=-2 CenterZ=0 NormalX=0 NormalY=0 NormalZ=1 AngleXU=0 Radius=1
  constraints (7):
    c: Diameter(g0) = 2
    c: Diameter(g1) = 2
    c: DistanceY(g-4,g-3) = 5.1
    c: DistanceY(g0,g-3) = 2.55
    c: DistanceY(g0,g1) = 0
    c: DistanceX(g1,g-5) = 0
    c: DistanceX(g0,g-3) = 16.7
FEATURE [PartDesign::Pad] Pad043
  BaseFeature = -> Pad042
  Direction = (0,0,-1)
  Length = 2.7
  Length2 = 10
  Profile = -> Sketch060
  ReferenceAxis = -> Sketch060 [N_Axis]
  Refine = true
  Suppressed = false
  Type = 0
FEATURE [Sketcher::SketchObject] Sketch061
  ArcFitTolerance = 1e-06
  AttachmentSupport = -> [Pad043]
  ExternalGeometry = -> [Pad043]
  FullyConstrained = true
  MakeInternals = false
  MapMode = 5
  Placement = pos=(0,0,2.75) rot=(1,0,0;3.14159rad)
  sketch-geometry (1):
    g0: Circle CenterX=75.717 CenterY=-12.7 CenterZ=0 NormalX=0 NormalY=0 NormalZ=1 AngleXU=0 Radius=1.5
  constraints (2):
    c: Coincident(g0,g-3)
    c: Diameter(g0) = 3
FEATURE [PartDesign::Pad] Pad044
  BaseFeature = -> Pad043
  Direction = (0,0,-1)
  Length = 5.93
  Length2 = 10
  Profile = -> Sketch061
  ReferenceAxis = -> Sketch061 [N_Axis]
  Refine = true
  Suppressed = false
  Type = 0
FEATURE [Sketcher::SketchObject] Sketch062
  ArcFitTolerance = 1e-06
  AttachmentSupport = -> [Pad044]
  ExternalGeometry = -> [Pad044]
  FullyConstrained = true
  MakeInternals = false
  MapMode = 5
  Placement = pos=(0,0,2.75) rot=(1,0,0;3.14159rad)
  sketch-geometry (4):
    g0: LineSegment StartX=74.0014 StartY=-13.0432 StartZ=0 EndX=75.717 EndY=-12.7 EndZ=0
    g1: LineSegment StartX=75.717 StartY=-12.7 StartZ=0 EndX=77.4631 EndY=-12.7 EndZ=0
    g2: LineSegment StartX=77.4631 StartY=-12.7 StartZ=0 EndX=77.2256 EndY=-13.5862 EndZ=0
    g3: ArcOfCircle CenterX=75.717 CenterY=-12.7 CenterZ=0 NormalX=0 NormalY=0 NormalZ=1 AngleXU=0 Radius=1.7496 StartAngle=3.33905 EndAngle=5.75207
  constraints (10):
    c: Coincident(g0,g-4)
    c: Coincident(g0,g-4)
    c: Coincident(g1,g0)
    c: PointOnObject(g1,g-5)
    c: Horizontal(g1)
    c: Coincident(g2,g1)
    c: Coincident(g2,g-5)
    c: Coincident(g3,g0)
    c: Coincident(g3,g2)
    c: Tangent(g3,g-4)
FEATURE [PartDesign::Pad] Pad045
  BaseFeature = -> Pad044
  Direction = (0,0,-1)
  Length = 1.425
  Length2 = 10
  Profile = -> Sketch062
  ReferenceAxis = -> Sketch062 [N_Axis]
  Refine = true
  Suppressed = false
  Type = 0
FEATURE [Sketcher::SketchObject] Sketch063
  ArcFitTolerance = 1e-06
  AttachmentSupport = -> [Pad045]
  ExternalGeometry = -> [Pad045]
  FullyConstrained = true
  MakeInternals = false
  MapMode = 5
  Placement = pos=(0,0,1.325) rot=(1,0,0;3.14159rad)
  sketch-geometry (1):
    g0: Circle CenterX=6.23499 CenterY=-7.25 CenterZ=0 NormalX=0 NormalY=0 NormalZ=1 AngleXU=0 Radius=1.15
  constraints (2):
    c: Coincident(g0,g-3)
    c: Diameter(g0) = 2.3
FEATURE [PartDesign::Pad] Pad046
  BaseFeature = -> Pad045
  Direction = (0,0,-1)
  Length = 4.5
  Length2 = 10
  Profile = -> Sketch063
  ReferenceAxis = -> Sketch063 [N_Axis]
  Refine = true
  Suppressed = false
  Type = 0
FEATURE [PartDesign::Pocket] Pocket020
  BaseFeature = -> Pad046
  Direction = (0,0,1)
  Length = 10
  Length2 = 5
  Profile = -> Pad046 [Face28,Face47]
  Refine = true
  Suppressed = false
  Type = 0
FEATURE [PartDesign::Pocket] Pocket021
  BaseFeature = -> Pocket020
  Direction = (0,0,1)
  Length = 2.7
  Length2 = 5
  Profile = -> Pocket020 [Face33,Face32]
  Refine = true
  Suppressed = false
  Type = 0
FEATURE [Sketcher::SketchObject] Sketch064
  ArcFitTolerance = 1e-06
  AttachmentSupport = -> [Pocket021]
  ExternalGeometry = -> [Pocket021]
  FullyConstrained = true
  MakeInternals = false
  MapMode = 5
  Placement = pos=(0,0,1.325) rot=(1,0,0;3.14159rad)
  sketch-geometry (2):
    g0: Circle CenterX=75.717 CenterY=-12.7 CenterZ=0 NormalX=0 NormalY=0 NormalZ=1 AngleXU=0 Radius=1.55
    g1: Circle CenterX=6.23499 CenterY=-7.25 CenterZ=0 NormalX=0 NormalY=0 NormalZ=1 AngleXU=0 Radius=1.2
  constraints (6):
    c: Diameter(g-3) = 3
    c: Coincident(g0,g-3)
    c: Diameter(g0) = 3.1
    c: Coincident(g1,g-4)
    c: Diameter(g-4) = 2.3
    c: Diameter(g1) = 2.4
FEATURE [PartDesign::Pocket] Pocket022
  BaseFeature = -> Pocket021
  Direction = (0,0,1)
  Length = 10
  Length2 = 5
  Profile = -> Sketch064
  ReferenceAxis = -> Sketch064 [N_Axis]
  Refine = true
  Suppressed = false
  Type = 0
FEATURE [PartDesign::Pocket] Pocket026
  BaseFeature = -> Pocket022
  Direction = (0,0,1)
  Length = 0.05
  Length2 = 5
  Profile = -> Pocket022 [Face2]
  Refine = true
  Suppressed = false
  Type = 0
FEATURE [PartDesign::Pocket] Pocket027
  BaseFeature = -> Pocket026
  Direction = (0,1,0)
  Length = 0.1
  Length2 = 5
  Profile = -> Pocket026 [Face50]
  Refine = true
  Suppressed = false
  Type = 0
FEATURE [PartDesign::Chamfer] Chamfer005
  Angle = 45
  Base = -> Pocket027 [Edge127]
  BaseFeature = -> Pocket027
  ChamferType = 0
  FlipDirection = false
  Refine = true
  Size = 0.249
  Size2 = 1
  SupportTransform = false
  Suppressed = false
  UseAllEdges = false
FEATURE [PartDesign::Body] Body003  label="Pre_Outer_Right_Crane_Boom"
  AllowCompound = false
  Group = -> [Binder001,Sketch050,Pad034,Sketch051,Pad035,Pad036,Sketch052,Pad037,Chamfer001,Sketch053,Pad038,Sketch054,Pad039,Sketch055,Pocket018,Sketch056,Pad040,Sketch057,Pocket019,Sketch058,Pad041,Sketch059,Pad042,Sketch060,Pad043,Sketch061,Pad044,Sketch062,Pad045,Sketch063,Pad046,Pocket020,Pocket021,Sketch064,Pocket022,Pocket026,Pocket027,Chamfer005]
  Origin = -> Origin003
  Tip = -> Chamfer005
COMPONENT P4 — recipe-attached ("Hook", modeled in this document).
Construction recipe (the document's own serialized feature program — sketch geometry with constraints, then the solid features built on it; lengths are millimeters unless a unit is written):

FEATURE [Sketcher::SketchObject] Sketch065
  ArcFitTolerance = 1e-06
  AttachmentSupport = -> [XY_Plane004]
  FullyConstrained = true
  MakeInternals = false
  MapMode = 5
  sketch-geometry (4):
    g0: ArcOfCircle CenterX=0 CenterY=0 CenterZ=0 NormalX=0 NormalY=0 NormalZ=1 AngleXU=0 Radius=2 StartAngle=5.38752 EndAngle=10.3204
    g1: LineSegment StartX=-1.25 StartY=-1.56125 StartZ=0 EndX=-1.25 EndY=-6.86125 EndZ=0
    g2: LineSegment StartX=-1.25 StartY=-6.86125 StartZ=0 EndX=1.25 EndY=-6.86125 EndZ=0
    g3: LineSegment StartX=1.25 StartY=-1.56125 StartZ=0 EndX=1.25 EndY=-6.86125 EndZ=0
  constraints (12):
    c: Coincident(g1,g0)
    c: Vertical(g1)
    c: Coincident(g2,g1)
    c: Horizontal(g2)
    c: Coincident(g3,g0)
    c: Coincident(g3,g2)
    c: Vertical(g3)
    c: Coincident(g0,g-1)
    c: Diameter(g0) = 4
    c: DistanceX(g2,g2) = 2.5
    c: DistanceY(g0,g0) = 0
    c: DistanceY(g3,g3) = 5.3
FEATURE [PartDesign::Pad] Pad047
  Direction = (0,0,1)
  Length = 2
  Length2 = 10
  Profile = -> Sketch065
  ReferenceAxis = -> Sketch065 [N_Axis]
  Refine = true
  Suppressed = false
  Type = 0
FEATURE [Sketcher::SketchObject] Sketch066
  ArcFitTolerance = 1e-06
  AttachmentSupport = -> [Pad047]
  FullyConstrained = true
  MakeInternals = false
  MapMode = 5
  Placement = pos=(0,0,2) rot=(0,0,1;0rad)
  sketch-geometry (1):
    g0: Circle CenterX=0 CenterY=0 CenterZ=0 NormalX=0 NormalY=0 NormalZ=1 AngleXU=0 Radius=0.95
  constraints (2):
    c: Coincident(g0,g-1)
    c: Diameter(g0) = 1.9
FEATURE [PartDesign::Pad] Pad048
  BaseFeature = -> Pad047
  Direction = (0,0,1)
  Length = 0.3
  Length2 = 10
  Profile = -> Sketch066
  ReferenceAxis = -> Sketch066 [N_Axis]
  Refine = true
  Suppressed = false
  Type = 0
FEATURE [Sketcher::SketchObject] Sketch067
  ArcFitTolerance = 1e-06
  AttachmentSupport = -> [Pad048]
  FullyConstrained = true
  MakeInternals = false
  MapMode = 5
  Placement = pos=(0,0,0) rot=(1,0,0;3.14159rad)
  sketch-geometry (1):
    g0: Circle CenterX=0 CenterY=0 CenterZ=0 NormalX=0 NormalY=0 NormalZ=1 AngleXU=0 Radius=0.95
  constraints (2):
    c: Coincident(g0,g-1)
    c: Diameter(g0) = 1.9
FEATURE [PartDesign::Pad] Pad049
  BaseFeature = -> Pad048
  Direction = (0,0,-1)
  Length = 0.3
  Length2 = 10
  Profile = -> Sketch067
  ReferenceAxis = -> Sketch067 [N_Axis]
  Refine = true
  Suppressed = false
  Type = 0
FEATURE [Sketcher::SketchObject] Sketch068
  ArcFitTolerance = 1e-06
  AttachmentOffset = pos=(0,0,0.5) rot=(0,0,1;0rad)
  AttachmentSupport = -> [Pad049]
  ExternalGeometry = -> [Pad049]
  FullyConstrained = true
  MakeInternals = false
  MapMode = 5
  Placement = pos=(0,0,-0.5) rot=(1,0,0;3.14159rad)
  sketch-geometry (6):
    g0: LineSegment StartX=-1.75 StartY=6.86125 StartZ=0 EndX=1.75 EndY=6.86125 EndZ=0
    g1: LineSegment StartX=1.75 StartY=6.86125 StartZ=0 EndX=2.5 EndY=9.2461 EndZ=0
    g2: LineSegment StartX=2.5 StartY=9.2461 StartZ=0 EndX=1.5 EndY=13.8612 EndZ=0
    g3: LineSegment StartX=-1.75 StartY=6.86125 StartZ=0 EndX=-2.5 EndY=9.2461 EndZ=0
    g4: LineSegment StartX=-2.5 StartY=9.2461 StartZ=0 EndX=-1.5 EndY=13.8612 EndZ=0
    g5: LineSegment StartX=-1.5 StartY=13.8612 StartZ=0 EndX=1.5 EndY=13.8612 EndZ=0
  constraints (19):
    c: Coincident(g1,g0)
    c: Coincident(g2,g1)
    c: Coincident(g3,g0)
    c: Coincident(g4,g3)
    c: Coincident(g5,g4)
    c: Coincident(g5,g2)
    c: Horizontal(g5)
    c: PointOnObject(g-3,g0)
    c: Horizontal(g0)
    c: DistanceX(g3,g1) = 5
    c: DistanceY(g3,g1) = 0
    c: DistanceX(g0,g-3) = 0.5
    c: DistanceX(g-3,g0) = 0.5
    c: DistanceX(g5,g5) = 3
    c: DistanceX(g-3,g-3) = 2.5
    c: DistanceX(g3,g-3) = 1.25
    c: DistanceY(g0,g4) = 7
    c: DistanceX(g-3,g2) = 0.25
    c: Distance(g1) = 2.5
FEATURE [PartDesign::Pad] Pad050
  BaseFeature = -> Pad049
  Direction = (0,0,-1)
  Length = 3
  Length2 = 10
  Profile = -> Sketch068
  ReferenceAxis = -> Sketch068 [N_Axis]
  Refine = true
  Reversed = true
  Suppressed = false
  Type = 0
FEATURE [Sketcher::SketchObject] Sketch069
  ArcFitTolerance = 1e-06
  AttachmentSupport = -> [Pad050]
  ExternalGeometry = -> [Pad050]
  FullyConstrained = true
  MakeInternals = false
  MapMode = 5
  Placement = pos=(0,0,-0.5) rot=(1,0,0;3.14159rad)
  sketch-geometry (2):
    g0: Circle CenterX=0 CenterY=8.36125 CenterZ=0 NormalX=0 NormalY=0 NormalZ=1 AngleXU=0 Radius=1
    g1: Circle CenterX=0 CenterY=12.3612 CenterZ=0 NormalX=0 NormalY=0 NormalZ=1 AngleXU=0 Radius=1
  constraints (6):
    c: PointOnObject(g0,g-2)
    c: PointOnObject(g1,g-2)
    c: Diameter(g1) = 2
    c: Diameter(g0) = 2
    c: DistanceY(g1,g-3) = 1.5
    c: DistanceY(g-5,g0) = 1.5
FEATURE [PartDesign::Pad] Pad051
  BaseFeature = -> Pad050
  Direction = (0,0,-1)
  Length = 0.5
  Length2 = 10
  Profile = -> Sketch069
  ReferenceAxis = -> Sketch069 [N_Axis]
  Refine = true
  Suppressed = false
  Type = 0
FEATURE [Sketcher::SketchObject] Sketch070
  ArcFitTolerance = 1e-06
  AttachmentSupport = -> [Pad051]
  ExternalGeometry = -> [Pad051]
  FullyConstrained = true
  MakeInternals = false
  MapMode = 5
  Placement = pos=(0,0,2.5) rot=(0,0,1;0rad)
  sketch-geometry (2):
    g0: Circle CenterX=0 CenterY=-12.3612 CenterZ=0 NormalX=0 NormalY=0 NormalZ=1 AngleXU=0 Radius=1
    g1: Circle CenterX=0 CenterY=-8.36125 CenterZ=0 NormalX=0 NormalY=0 NormalZ=1 AngleXU=0 Radius=1
  constraints (6):
    c: PointOnObject(g0,g-2)
    c: PointOnObject(g1,g-2)
    c: Diameter(g1) = 2
    c: Diameter(g0) = 2
    c: DistanceY(g-4,g0) = 1.5
    c: DistanceY(g1,g-3) = 1.5
FEATURE [PartDesign::Pad] Pad052
  BaseFeature = -> Pad051
  Direction = (0,0,1)
  Length = 0.5
  Length2 = 10
  Profile = -> Sketch070
  ReferenceAxis = -> Sketch070 [N_Axis]
  Refine = true
  Suppressed = false
  Type = 0
FEATURE [Sketcher::SketchObject] Sketch071
  ArcFitTolerance = 1e-06
  AttachmentOffset = pos=(0,0,-0.5) rot=(0,0,1;0rad)
  AttachmentSupport = -> [Pad052]
  ExternalGeometry = -> [Pad052]
  FullyConstrained = true
  MakeInternals = false
  MapMode = 5
  Placement = pos=(0,0,0) rot=(1,0,0;3.14159rad)
  sketch-geometry (18):
    g0: LineSegment StartX=-1.25 StartY=13.8612 StartZ=0 EndX=1.25 EndY=13.8612 EndZ=0
    g1: LineSegment StartX=1.25 StartY=13.8612 StartZ=0 EndX=1.25 EndY=15.1612 EndZ=0
    g2: LineSegment StartX=-1.25 StartY=13.8612 StartZ=0 EndX=-1.25 EndY=15.1612 EndZ=0
    g3: LineSegment StartX=-0.775 StartY=18.7362 StartZ=0 EndX=-1.83566 EndY=17.6756 EndZ=0
    g4: ArcOfCircle CenterX=-2.18921 CenterY=18.0291 CenterZ=0 NormalX=0 NormalY=0 NormalZ=1 AngleXU=0 Radius=0.5 StartAngle=2.35619 EndAngle=5.49779
    g5: LineSegment StartX=1.25 StartY=15.1612 StartZ=0 EndX=1.39304 EndY=15.3043 EndZ=0
    g6: LineSegment StartX=-1.25 StartY=15.1612 StartZ=0 EndX=0.775 EndY=17.1862 EndZ=0
    g7: ArcOfCircle CenterX=0 CenterY=17.9612 CenterZ=0 NormalX=0 NormalY=0 NormalZ=1 AngleXU=0 Radius=1.09602 StartAngle=5.49779 EndAngle=8.63938
    g8: ArcOfCircle CenterX=0 CenterY=17.9612 CenterZ=0 NormalX=0 NormalY=0 NormalZ=1 AngleXU=0 Radius=3 StartAngle=5.19529 EndAngle=8.75521
    g9: LineSegment [constr] StartX=0 StartY=20.9612 StartZ=0 EndX=4 EndY=20.9612 EndZ=0
    g10: LineSegment [constr] StartX=4 StartY=20.9612 StartZ=0 EndX=4 EndY=13.8612 EndZ=0
    g11: LineSegment [constr] StartX=1.5 StartY=13.8612 StartZ=0 EndX=4 EndY=13.8612 EndZ=0
    g12: LineSegment [constr] StartX=0.775 StartY=17.1862 StartZ=0 EndX=0 EndY=17.9612 EndZ=0
    g13: LineSegment [constr] StartX=0 StartY=17.9612 StartZ=0 EndX=-0.775 EndY=18.7362 EndZ=0
    g14: LineSegment StartX=-2.35226 StartY=18.5732 StartZ=0 EndX=-2.54277 EndY=18.3827 EndZ=0
    g15: LineSegment [constr] StartX=-1.83566 StartY=17.6756 StartZ=0 EndX=-2.18921 EndY=18.0291 EndZ=0
    g16: LineSegment [constr] StartX=-2.18921 StartY=18.0291 StartZ=0 EndX=-2.54277 EndY=18.3827 EndZ=0
    g17: LineSegment StartX=-2.35226 StartY=19.8232 StartZ=0 EndX=-2.35226 EndY=18.5732 EndZ=0
  constraints (52):
    c: PointOnObject(g0,g-3)
    c: PointOnObject(g0,g-3)
    c: Coincident(g1,g0)
    c: Vertical(g1)
    c: Coincident(g2,g0)
    c: Coincident(g4,g3)
    c: Coincident(g5,g1)
    c: Coincident(g6,g2)
    c: Coincident(g7,g3)
    c: Coincident(g7,g6)
    c: Coincident(g8,g5)
    c: DistanceX(g0,g0) = 2.5
    c: DistanceX(g-3,g0) = 0.25
    c: Vertical(g2)
    c: Parallel(g5,g6)
    c: Angle(g1,g5) = 2.35619
    c: DistanceY(g2,g1) = 0
    c: PointOnObject(g8,g-2)
    c: Coincident(g7,g8)
    c: PointOnObject(g9,g8)
    c: Horizontal(g9)
    c: Coincident(g10,g9)
    c: Vertical(g10)
    c: Coincident(g11,g-3)
    c: Coincident(g11,g10)
    c: DistanceY(g10,g10) = 7.1
    c: Horizontal(g11)
    c: DistanceX(g9,g9) = 4
    c: PointOnObject(g9,g-2)
    c: Radius(g8) = 3
    c: Diameter(g4) = 1
    c: DistanceY(g1,g1) = 1.3
    c: Coincident(g12,g6)
    c: Coincident(g12,g7)
    c: Coincident(g13,g7)
    c: Coincident(g13,g3)
    c: Angle(g13,g12) = 3.14159
    c: Angle(g12,g6) = 1.5708
    c: Coincident(g14,g4)
    c: Parallel(g3,g14)
    c: Angle(g3,g13) = 1.5708
    c: Coincident(g15,g3)
    c: Coincident(g15,g4)
    c: Coincident(g16,g4)
    c: Coincident(g16,g4)
    c: Angle(g16,g15) = 3.14159
    c: Angle(g3,g15) = 1.5708
    c: Vertical(g17)
    c: Coincident(g14,g17)
    c: Coincident(g8,g17)
    c: DistanceY(g17,g17) = 1.25
    c: Distance(g3) = 1.5
FEATURE [PartDesign::Pad] Pad053
  BaseFeature = -> Pad052
  Direction = (0,0,-1)
  Length = 2
  Length2 = 10
  Profile = -> Sketch071
  ReferenceAxis = -> Sketch071 [N_Axis]
  Refine = true
  Reversed = true
  Suppressed = false
  Type = 0
FEATURE [PartDesign::Fillet] Fillet001
  Base = -> Pad053 [Edge66,Edge69,Edge57,Edge59,Edge68,Edge58,Edge54,Edge55,Edge67,Edge56,Edge74,Edge64,Edge70,Edge60]
  BaseFeature = -> Pad053
  Radius = 0.5
  Refine = true
  SupportTransform = false
  Suppressed = false
  UseAllEdges = false
FEATURE [PartDesign::Body] Body004  label="Hook"
  AllowCompound = false
  Group = -> [Sketch065,Pad047,Sketch066,Pad048,Sketch067,Pad049,Sketch068,Pad050,Sketch069,Pad051,Sketch070,Pad052,Sketch071,Pad053,Fillet001]
  Origin = -> Origin004
  Placement = pos=(19.06,-40.35,21.85) rot=(0.57735,-0.57735,-0.57735;2.0944rad)
  Tip = -> Fillet001
COMPONENT P5 — recipe-attached ("Arm_Link", modeled in this document).
Construction recipe (the document's own serialized feature program — sketch geometry with constraints, then the solid features built on it; lengths are millimeters unless a unit is written):

FEATURE [Sketcher::SketchObject] Sketch072
  ArcFitTolerance = 1e-06
  AttachmentSupport = -> [XY_Plane005]
  FullyConstrained = true
  MakeInternals = false
  MapMode = 5
  sketch-geometry (1):
    g0: Circle CenterX=0 CenterY=0 CenterZ=0 NormalX=0 NormalY=0 NormalZ=1 AngleXU=0 Radius=2.55
  constraints (2):
    c: Coincident(g0,g-1)
    c: Diameter(g0) = 5.1
FEATURE [PartDesign::Pad] Pad054
  Direction = (0,0,1)
  Length = 6
  Length2 = 10
  Profile = -> Sketch072
  ReferenceAxis = -> Sketch072 [N_Axis]
  Refine = true
  Suppressed = false
  Type = 0
FEATURE [Sketcher::SketchObject] Sketch073
  ArcFitTolerance = 1e-06
  AttachmentOffset = pos=(0,0,-1.05) rot=(0,0,1;0rad)
  AttachmentSupport = -> [Pad054]
  ExternalGeometry = -> [Pad054]
  FullyConstrained = false
  MakeInternals = false
  MapMode = 5
  Placement = pos=(0,0,1.05) rot=(1,0,0;3.14159rad)
  sketch-geometry (5):
    g0: LineSegment StartX=1.64317 StartY=1.95 StartZ=0 EndX=12.041 EndY=1.95 EndZ=0
    g1: LineSegment StartX=12.041 StartY=1.95 StartZ=0 EndX=12.041 EndY=-1.95 EndZ=0
    g2: LineSegment StartX=12.041 StartY=-1.95 StartZ=0 EndX=1.64317 EndY=-1.95 EndZ=0
    g3: ArcOfCircle CenterX=-0.0255644 CenterY=0 CenterZ=0 NormalX=0 NormalY=0 NormalZ=1 AngleXU=0 Radius=2.56655 StartAngle=5.42022 EndAngle=7.14615
    g4: LineSegment [constr] StartX=2.54098 StartY=0 StartZ=0 EndX=12.041 EndY=0 EndZ=0
  constraints (15):
    c: PointOnObject(g0,g-3)
    c: Horizontal(g0)
    c: Coincident(g1,g0)
    c: Vertical(g1)
    c: Coincident(g2,g1)
    c: PointOnObject(g2,g-3)
    c: Horizontal(g2)
    c: Coincident(g3,g0)
    c: Coincident(g3,g2)
    c: DistanceY(g3,g0) = 1.95
    c: DistanceY(g1,g1) = 3.9
    c: PointOnObject(g4,g3)
    c: Symmetric(g1,g1,g4)
    c: Horizontal(g4)
    c: DistanceX(g4,g4) = 9.5
FEATURE [PartDesign::Pad] Pad055
  BaseFeature = -> Pad054
  Direction = (0,0,-1)
  Length = 3.9
  Length2 = 10
  Profile = -> Sketch073
  ReferenceAxis = -> Sketch073 [N_Axis]
  Refine = true
  Reversed = true
  Suppressed = false
  Type = 0
FEATURE [PartDesign::Fillet] Fillet002
  Base = -> Pad055 [Edge16,Edge18,Edge12,Edge14,Edge17,Edge11,Edge15,Edge13,Edge7]
  BaseFeature = -> Pad055
  Radius = 0.5
  Refine = true
  SupportTransform = false
  Suppressed = false
  UseAllEdges = false
FEATURE [Sketcher::SketchObject] Sketch074
  ArcFitTolerance = 1e-06
  AttachmentSupport = -> [Fillet002]
  FullyConstrained = true
  MakeInternals = false
  MapMode = 5
  Placement = pos=(0,0,0) rot=(1,0,0;3.14159rad)
  sketch-geometry (1):
    g0: Circle CenterX=0 CenterY=0 CenterZ=0 NormalX=0 NormalY=0 NormalZ=1 AngleXU=0 Radius=0.75
  constraints (2):
    c: Coincident(g0,g-1)
    c: Diameter(g0) = 1.5
FEATURE [PartDesign::Pocket] Pocket028
  BaseFeature = -> Fillet002
  Direction = (0,0,1)
  Length = 5
  Length2 = 5
  Profile = -> Sketch074
  ReferenceAxis = -> Sketch074 [N_Axis]
  Refine = true
  Suppressed = false
  Type = 0
FEATURE [Sketcher::SketchObject] Sketch075
  ArcFitTolerance = 1e-06
  AttachmentSupport = -> [Pocket028]
  ExternalGeometry = -> [Pocket028]
  FullyConstrained = true
  MakeInternals = false
  MapMode = 5
  Placement = pos=(0,0,4.95) rot=(0,0,1;0rad)
  sketch-geometry (4):
    g0: LineSegment StartX=11.541 StartY=0.75 StartZ=0 EndX=3.04098 EndY=0.75 EndZ=0
    g1: LineSegment StartX=3.04098 StartY=0.75 StartZ=0 EndX=3.04098 EndY=-0.75 EndZ=0
    g2: LineSegment StartX=3.04098 StartY=-0.75 StartZ=0 EndX=11.541 EndY=-0.75 EndZ=0
    g3: LineSegment StartX=11.541 StartY=-0.75 StartZ=0 EndX=11.541 EndY=0.75 EndZ=0
  constraints (12):
    c: Coincident(g0,g1)
    c: Coincident(g1,g2)
    c: Coincident(g2,g3)
    c: Coincident(g3,g0)
    c: Horizontal(g0)
    c: Horizontal(g2)
    c: Vertical(g1)
    c: Vertical(g3)
    c: PointOnObject(g0,g-3)
    c: DistanceX(g0,g0) = 8.5
    c: DistanceY(g1,g1) = 1.5
    c: DistanceY(g-4,g0) = 0.75
FEATURE [PartDesign::Pad] Pad056
  BaseFeature = -> Pocket028
  Direction = (0,0,1)
  Length = 0.1
  Length2 = 10
  Profile = -> Sketch075
  ReferenceAxis = -> Sketch075 [N_Axis]
  Refine = true
  Suppressed = false
  Type = 0
FEATURE [Sketcher::SketchObject] Sketch076
  ArcFitTolerance = 1e-06
  AttachmentSupport = -> [Pad056]
  ExternalGeometry = -> [Pad056]
  FullyConstrained = true
  MakeInternals = false
  MapMode = 5
  Placement = pos=(0,-0.75,0) rot=(1,0,0;1.5708rad)
  sketch-geometry (3):
    g0: LineSegment StartX=11.541 StartY=5.05 StartZ=0 EndX=11.541 EndY=4.95 EndZ=0
    g1: LineSegment StartX=11.541 StartY=5.05 StartZ=0 EndX=11.441 EndY=5.05 EndZ=0
    g2: LineSegment StartX=11.541 StartY=4.95 StartZ=0 EndX=11.441 EndY=5.05 EndZ=0
  constraints (7):
    c: Coincident(g0,g-4)
    c: Coincident(g0,g-3)
    c: Coincident(g1,g0)
    c: PointOnObject(g1,g-4)
    c: Coincident(g2,g0)
    c: Coincident(g2,g1)
    c: Angle(g0,g2) = 0.785398
FEATURE [PartDesign::Pocket] Pocket029
  BaseFeature = -> Pad056
  Direction = (0,1,-2e-16)
  Length = 5
  Length2 = 5
  Profile = -> Sketch076
  ReferenceAxis = -> Sketch076 [N_Axis]
  Refine = true
  Suppressed = false
  Type = 0
FEATURE [PartDesign::Body] Body005  label="Arm_Link"
  AllowCompound = false
  Group = -> [Sketch072,Pad054,Sketch073,Pad055,Fillet002,Sketch074,Pocket028,Sketch075,Pad056,Sketch076,Pocket029]
  Origin = -> Origin005
  Placement = pos=(4,5.9,2) rot=(0,0,1;3.14159rad)
  Tip = -> Pocket029
COMPONENT P6 — recipe-attached ("Waist_Link", modeled in this document).
Construction recipe (the document's own serialized feature program — sketch geometry with constraints, then the solid features built on it; lengths are millimeters unless a unit is written):

FEATURE [Sketcher::SketchObject] Sketch077
  ArcFitTolerance = 1e-06
  AttachmentSupport = -> [XY_Plane006]
  FullyConstrained = true
  MakeInternals = false
  MapMode = 5
  sketch-geometry (4):
    g0: ArcOfCircle CenterX=0 CenterY=0 CenterZ=0 NormalX=0 NormalY=0 NormalZ=1 AngleXU=0 Radius=5 StartAngle=1.5708 EndAngle=4.71239
    g1: ArcOfCircle CenterX=36 CenterY=2.24e-14 CenterZ=0 NormalX=0 NormalY=0 NormalZ=1 AngleXU=0 Radius=5 StartAngle=4.71239 EndAngle=7.85398
    g2: LineSegment StartX=-2.872e-13 StartY=5 StartZ=0 EndX=36 EndY=5 EndZ=0
    g3: LineSegment StartX=-9e-16 StartY=-5 StartZ=0 EndX=36 EndY=-5 EndZ=0
  constraints (9):
    c: Tangent(g0,g2) = 1.5708
    c: Tangent(g0,g3) = -1.5708
    c: Tangent(g1,g2) = 1.5708
    c: Tangent(g1,g3) = -1.5708
    c: Equal(g0,g1)
    c: Horizontal(g3)
    c: Coincident(g0,g-1)
    c: Diameter(g0) = 10
    c: DistanceX(g0,g1) = 36
FEATURE [PartDesign::Pad] Pad057
  Direction = (0,0,1)
  Length = 3.7
  Length2 = 10
  Profile = -> Sketch077
  ReferenceAxis = -> Sketch077 [N_Axis]
  Refine = true
  Suppressed = false
  Type = 0
FEATURE [Sketcher::SketchObject] Sketch078
  ArcFitTolerance = 1e-06
  AttachmentSupport = -> [Pad057]
  ExternalGeometry = -> [Pad057]
  FullyConstrained = true
  MakeInternals = false
  MapMode = 5
  Placement = pos=(0,0,3.7) rot=(0,0,1;0rad)
  sketch-geometry (8):
    g0: ArcOfCircle CenterX=0 CenterY=0 CenterZ=0 NormalX=0 NormalY=0 NormalZ=1 AngleXU=0 Radius=3.45 StartAngle=1.5708 EndAngle=4.71239
    g1: ArcOfCircle CenterX=12.9 CenterY=0 CenterZ=0 NormalX=0 NormalY=0 NormalZ=1 AngleXU=0 Radius=3.45 StartAngle=4.71239 EndAngle=7.85398
    g2: LineSegment StartX=-6e-16 StartY=3.45 StartZ=0 EndX=12.9 EndY=3.45 EndZ=0
    g3: LineSegment StartX=-6e-16 StartY=-3.45 StartZ=0 EndX=12.9 EndY=-3.45 EndZ=0
    g4: ArcOfCircle CenterX=36 CenterY=2.24e-14 CenterZ=0 NormalX=0 NormalY=0 NormalZ=1 AngleXU=0 Radius=3.45 StartAngle=4.71239 EndAngle=7.85398
    g5: ArcOfCircle CenterX=23.1 CenterY=2.28e-14 CenterZ=0 NormalX=0 NormalY=0 NormalZ=1 AngleXU=0 Radius=3.45 StartAngle=1.5708 EndAngle=4.71239
    g6: LineSegment StartX=36 StartY=-3.45 StartZ=0 EndX=23.1 EndY=-3.45 EndZ=0
    g7: LineSegment StartX=36 StartY=3.45 StartZ=0 EndX=23.1 EndY=3.45 EndZ=0
  constraints (18):
    c: Tangent(g0,g2) = 1.5708
    c: Tangent(g0,g3) = -1.5708
    c: Tangent(g1,g2) = 1.5708
    c: Tangent(g1,g3) = -1.5708
    c: Equal(g0,g1)
    c: Horizontal(g3)
    c: Coincident(g0,g-1)
    c: Tangent(g4,g6) = 1.5708
    c: Tangent(g4,g7) = -1.5708
    c: Tangent(g5,g6) = 1.5708
    c: Tangent(g5,g7) = -1.5708
    c: Equal(g4,g5)
    c: Horizontal(g7)
    c: Diameter(g0) = 6.9
    c: Diameter(g5) = 6.9
    c: DistanceX(g0,g1) = 12.9
    c: DistanceX(g5,g4) = 12.9
    c: Coincident(g4,g-3)
FEATURE [PartDesign::Pocket] Pocket030
  BaseFeature = -> Pad057
  Direction = (0,0,-1)
  Length = 1.5
  Length2 = 5
  Profile = -> Sketch078
  ReferenceAxis = -> Sketch078 [N_Axis]
  Refine = true
  Suppressed = false
  Type = 0
FEATURE [Sketcher::SketchObject] Sketch079
  ArcFitTolerance = 1e-06
  AttachmentSupport = -> [Pocket030]
  ExternalGeometry = -> [Pocket030]
  FullyConstrained = true
  MakeInternals = false
  MapMode = 5
  Placement = pos=(0,0,2.2) rot=(0,0,1;0rad)
  sketch-geometry (8):
    g0: ArcOfCircle CenterX=0 CenterY=0 CenterZ=0 NormalX=0 NormalY=0 NormalZ=1 AngleXU=0 Radius=2.45 StartAngle=1.5708 EndAngle=4.71239
    g1: ArcOfCircle CenterX=12.9 CenterY=0 CenterZ=0 NormalX=0 NormalY=0 NormalZ=1 AngleXU=0 Radius=2.45 StartAngle=4.71239 EndAngle=7.85398
    g2: LineSegment StartX=-2.16e-14 StartY=2.45 StartZ=0 EndX=12.9 EndY=2.45 EndZ=0
    g3: LineSegment StartX=-2.22e-14 StartY=-2.45 StartZ=0 EndX=12.9 EndY=-2.45 EndZ=0
    g4: ArcOfCircle CenterX=36 CenterY=2.24e-14 CenterZ=0 NormalX=0 NormalY=0 NormalZ=1 AngleXU=0 Radius=2.45 StartAngle=4.71239 EndAngle=7.85398
    g5: ArcOfCircle CenterX=23.1 CenterY=2.28e-14 CenterZ=0 NormalX=0 NormalY=0 NormalZ=1 AngleXU=0 Radius=2.45 StartAngle=1.5708 EndAngle=4.71239
    g6: LineSegment StartX=36 StartY=-2.45 StartZ=0 EndX=23.1 EndY=-2.45 EndZ=0
    g7: LineSegment StartX=36 StartY=2.45 StartZ=0 EndX=23.1 EndY=2.45 EndZ=0
  constraints (16):
    c: Tangent(g0,g2) = 1.5708
    c: Tangent(g0,g3) = -1.5708
    c: Tangent(g1,g2) = 1.5708
    c: Tangent(g1,g3) = -1.5708
    c: Equal(g0,g1)
    c: Coincident(g0,g-1)
    c: Tangent(g4,g6) = 1.5708
    c: Tangent(g4,g7) = -1.5708
    c: Tangent(g5,g6) = 1.5708
    c: Tangent(g5,g7) = -1.5708
    c: Equal(g4,g5)
    c: Coincident(g4,g-3)
    c: Diameter(g1) = 4.9
    c: Diameter(g5) = 4.9
    c: Coincident(g1,g-4)
    c: Coincident(g5,g-5)
FEATURE [PartDesign::Pocket] Pocket031
  BaseFeature = -> Pocket030
  Direction = (0,0,-1)
  Length = 5
  Length2 = 5
  Profile = -> Sketch079
  ReferenceAxis = -> Sketch079 [N_Axis]
  Refine = true
  Suppressed = false
  Type = 0
FEATURE [PartDesign::Body] Body006  label="Waist_Link"
  AllowCompound = false
  Group = -> [Sketch077,Pad057,Sketch078,Pocket030,Sketch079,Pocket031]
  Origin = -> Origin006
  Placement = pos=(18,-18.15,-2) rot=(0,0,-1;4.71239rad)
  Tip = -> Pocket031
